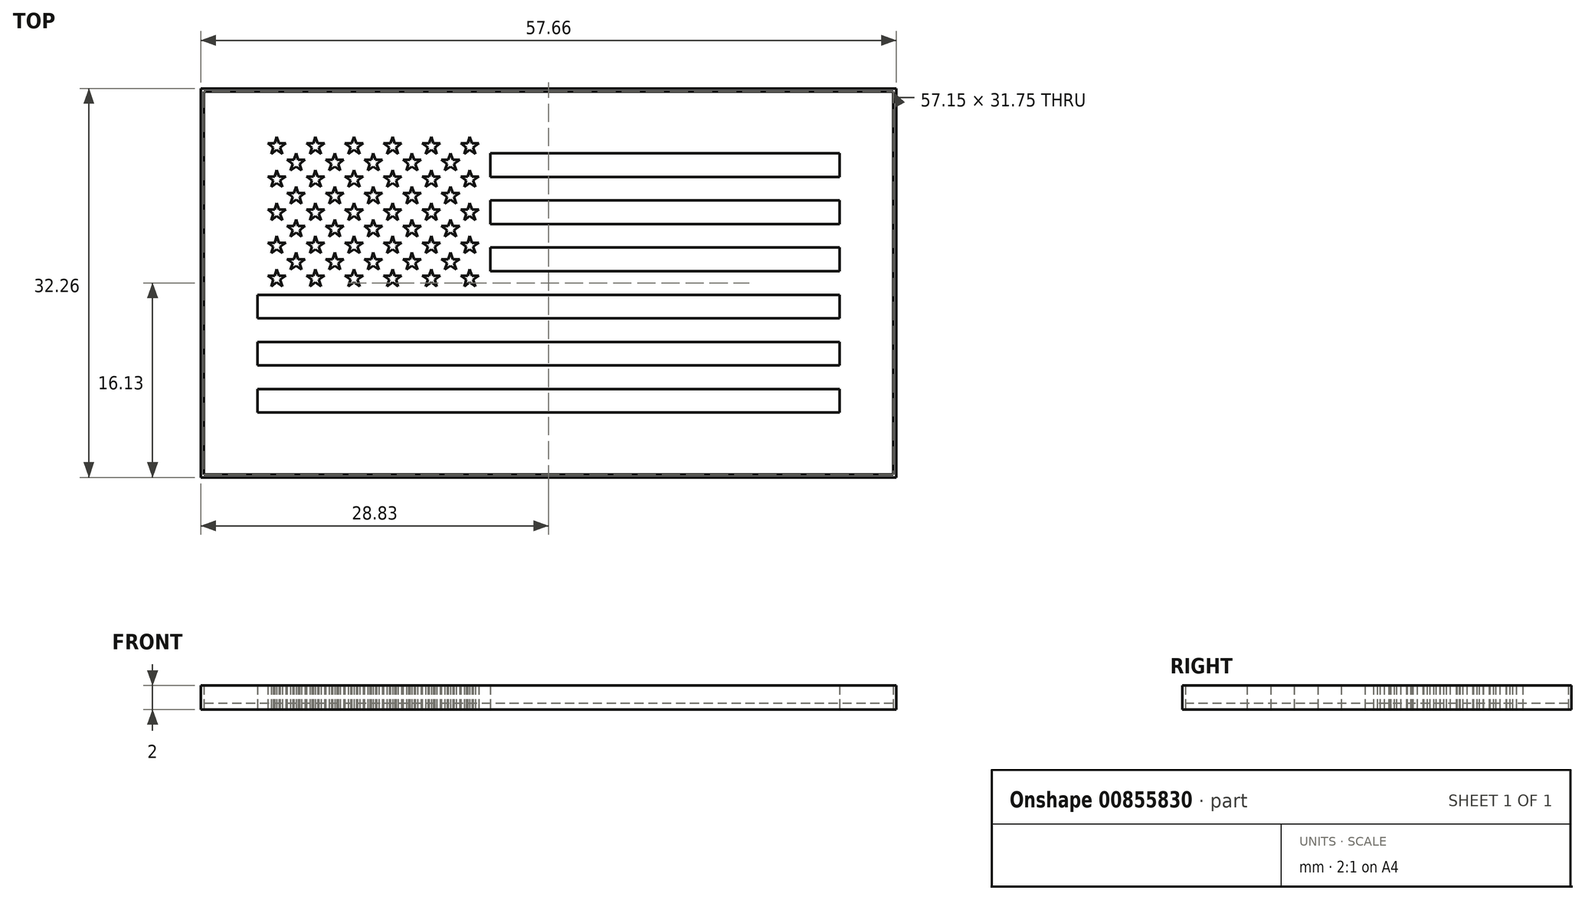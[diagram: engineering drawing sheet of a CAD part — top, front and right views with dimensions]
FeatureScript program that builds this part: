
annotation { "Feature Type Name" : "Feature", "Feature Type Description" : "" }
export const myFeature = defineFeature(function(context is Context, id is Id, definition is map)
    precondition{}
    {
        {
            var Q0;
            Q0=qCreatedBy(makeId("Top.planeOp"),FACE);
            var sketch = newSketch(context, id + "F0", { "sketchPlane" : qUnion([Q0])});
            skLineSegment(sketch, "E0.rect.bottom", {"start": v(24.13, 12.7) * mm, "end": v(-24.13, 12.7) * mm});
            skLineSegment(sketch, "E0.rect.top", {"start": v(24.13, -12.7) * mm, "end": v(-24.13, -12.7) * mm});
            skLineSegment(sketch, "E0.rect.left", {"start": v(24.13, 12.7) * mm, "end": v(24.13, -12.7) * mm});
            skLineSegment(sketch, "E0.rect.right", {"start": v(-24.13, 12.7) * mm, "end": v(-24.13, -12.7) * mm});
            skPoint(sketch, "E0.rect.middle", {"position": v(0, 0) * mm});
            skLineSegment(sketch, "E1.bottom", {"start": v(-24.13, 12.7) * mm, "end": v(-4.83, 12.7) * mm});
            skLineSegment(sketch, "E1.top", {"start": v(-24.13, -0.98) * mm, "end": v(-4.83, -0.98) * mm});
            skLineSegment(sketch, "E1.left", {"start": v(-24.13, 12.7) * mm, "end": v(-24.13, -0.98) * mm});
            skLineSegment(sketch, "E1.right", {"start": v(-4.83, 12.7) * mm, "end": v(-4.83, -0.98) * mm});
            skLineSegment(sketch, "E2.bottom", {"start": v(-4.83, 12.7) * mm, "end": v(24.13, 12.7) * mm});
            skLineSegment(sketch, "E2.top", {"start": v(-4.83, 10.75) * mm, "end": v(24.13, 10.75) * mm});
            skLineSegment(sketch, "E2.left", {"start": v(-4.83, 12.7) * mm, "end": v(-4.83, 10.75) * mm});
            skLineSegment(sketch, "E2.right", {"start": v(24.13, 12.7) * mm, "end": v(24.13, 10.75) * mm});
            skLineSegment(sketch, "E3.MirrorCS", {"start": v(-4.83, 8.8) * mm, "end": v(24.13, 8.8) * mm});
            skLineSegment(sketch, "E4.MirrorCS", {"start": v(-4.83, 6.84) * mm, "end": v(24.13, 6.84) * mm});
            skLineSegment(sketch, "E5.MirrorCS", {"start": v(-4.83, 4.89) * mm, "end": v(24.13, 4.89) * mm});
            skLineSegment(sketch, "E6.MirrorCS", {"start": v(-4.83, 2.93) * mm, "end": v(24.13, 2.93) * mm});
            skLineSegment(sketch, "E7.MirrorCS", {"start": v(-4.83, 0.98) * mm, "end": v(24.13, 0.98) * mm});
            skLineSegment(sketch, "E8.MirrorCS", {"start": v(-4.83, -0.97) * mm, "end": v(24.13, -0.97) * mm});
            skLineSegment(sketch, "E9.bottom", {"start": v(-24.13, -0.98) * mm, "end": v(24.13, -0.98) * mm});
            skLineSegment(sketch, "E9.top", {"start": v(-24.13, -2.93) * mm, "end": v(24.13, -2.93) * mm});
            skLineSegment(sketch, "E9.left", {"start": v(-24.13, -0.98) * mm, "end": v(-24.13, -2.93) * mm});
            skLineSegment(sketch, "E9.right", {"start": v(24.13, -0.98) * mm, "end": v(24.13, -2.93) * mm});
            skLineSegment(sketch, "E10.MirrorCS", {"start": v(-24.13, -4.88) * mm, "end": v(24.13, -4.88) * mm});
            skLineSegment(sketch, "E11.MirrorCS", {"start": v(-24.13, -6.84) * mm, "end": v(24.13, -6.84) * mm});
            skLineSegment(sketch, "E12.MirrorCS", {"start": v(-24.13, -8.8) * mm, "end": v(24.13, -8.8) * mm});
            skLineSegment(sketch, "E13.MirrorCS", {"start": v(-24.13, -10.74) * mm, "end": v(24.13, -10.74) * mm});
            skLineSegment(sketch, "E14.bottom", {"start": v(-24.13, 12.7) * mm, "end": v(-22.53, 12.7) * mm});
            skLineSegment(sketch, "E14.left", {"start": v(-24.13, 12.7) * mm, "end": v(-24.13, 11.33) * mm});
            skPoint(sketch, "E15.cCircle.perimeterSnap0", {"position": v(-22.53, 12.01) * mm});
            skPoint(sketch, "E15.0.startSnap0", {"position": v(-22.53, 12.01) * mm});
            skLineSegment(sketch, "E16", {"start": v(-22.53, 12.12) * mm, "end": v(-22.35, 11.57) * mm});
            skLineSegment(sketch, "E17", {"start": v(-21.78, 11.57) * mm, "end": v(-22.35, 11.57) * mm});
            skLineSegment(sketch, "E18", {"start": v(-23, 10.7) * mm, "end": v(-22.82, 11.24) * mm});
            skLineSegment(sketch, "E19", {"start": v(-23.28, 11.57) * mm, "end": v(-22.82, 11.24) * mm});
            skLineSegment(sketch, "E20", {"start": v(-21.78, 11.57) * mm, "end": v(-22.24, 11.24) * mm});
            skLineSegment(sketch, "E21.trimOffspring", {"start": v(-22.24, 11.24) * mm, "end": v(-22.07, 10.7) * mm});
            skLineSegment(sketch, "E22.trimOffspring", {"start": v(-22.53, 11.03) * mm, "end": v(-23, 10.7) * mm});
            skLineSegment(sketch, "E23.trimOffspring", {"start": v(-22.53, 11.03) * mm, "end": v(-22.07, 10.7) * mm});
            skLineSegment(sketch, "E24.trimOffspring", {"start": v(-22.7, 11.57) * mm, "end": v(-22.53, 12.12) * mm});
            skLineSegment(sketch, "E25.trimOffspring", {"start": v(-22.7, 11.57) * mm, "end": v(-23.28, 11.57) * mm});
            skLineSegment(sketch, "E26.0.1.0", {"start": v(-22.53, 9.37) * mm, "end": v(-22.35, 8.83) * mm});
            skLineSegment(sketch, "E26.0.1.1", {"start": v(-21.78, 8.83) * mm, "end": v(-22.35, 8.83) * mm});
            skLineSegment(sketch, "E26.0.1.2", {"start": v(-21.78, 8.83) * mm, "end": v(-22.24, 8.5) * mm});
            skLineSegment(sketch, "E26.0.1.3", {"start": v(-22.24, 8.5) * mm, "end": v(-22.07, 7.95) * mm});
            skLineSegment(sketch, "E26.0.1.4", {"start": v(-22.53, 8.28) * mm, "end": v(-22.07, 7.95) * mm});
            skLineSegment(sketch, "E26.0.1.5", {"start": v(-22.53, 8.28) * mm, "end": v(-23, 7.95) * mm});
            skLineSegment(sketch, "E26.0.1.6", {"start": v(-23, 7.95) * mm, "end": v(-22.82, 8.5) * mm});
            skLineSegment(sketch, "E26.0.1.7", {"start": v(-23.28, 8.83) * mm, "end": v(-22.82, 8.5) * mm});
            skLineSegment(sketch, "E26.0.1.8", {"start": v(-22.7, 8.83) * mm, "end": v(-22.53, 9.37) * mm});
            skLineSegment(sketch, "E26.0.1.9", {"start": v(-22.7, 8.83) * mm, "end": v(-23.28, 8.83) * mm});
            skLineSegment(sketch, "E26.0.2.0", {"start": v(-22.53, 6.63) * mm, "end": v(-22.35, 6.09) * mm});
            skLineSegment(sketch, "E26.0.2.1", {"start": v(-21.78, 6.09) * mm, "end": v(-22.35, 6.09) * mm});
            skLineSegment(sketch, "E26.0.2.2", {"start": v(-21.78, 6.09) * mm, "end": v(-22.24, 5.75) * mm});
            skLineSegment(sketch, "E26.0.2.3", {"start": v(-22.24, 5.75) * mm, "end": v(-22.07, 5.2) * mm});
            skLineSegment(sketch, "E26.0.2.4", {"start": v(-22.53, 5.54) * mm, "end": v(-22.07, 5.2) * mm});
            skLineSegment(sketch, "E26.0.2.5", {"start": v(-22.53, 5.54) * mm, "end": v(-23, 5.2) * mm});
            skLineSegment(sketch, "E26.0.2.6", {"start": v(-23, 5.2) * mm, "end": v(-22.82, 5.75) * mm});
            skLineSegment(sketch, "E26.0.2.7", {"start": v(-23.28, 6.09) * mm, "end": v(-22.82, 5.75) * mm});
            skLineSegment(sketch, "E26.0.2.8", {"start": v(-22.7, 6.09) * mm, "end": v(-22.53, 6.63) * mm});
            skLineSegment(sketch, "E26.0.2.9", {"start": v(-22.7, 6.09) * mm, "end": v(-23.28, 6.09) * mm});
            skLineSegment(sketch, "E26.0.3.0", {"start": v(-22.53, 3.89) * mm, "end": v(-22.35, 3.34) * mm});
            skLineSegment(sketch, "E26.0.3.1", {"start": v(-21.78, 3.34) * mm, "end": v(-22.35, 3.34) * mm});
            skLineSegment(sketch, "E26.0.3.2", {"start": v(-21.78, 3.34) * mm, "end": v(-22.24, 3) * mm});
            skLineSegment(sketch, "E26.0.3.3", {"start": v(-22.24, 3) * mm, "end": v(-22.07, 2.46) * mm});
            skLineSegment(sketch, "E26.0.3.4", {"start": v(-22.53, 2.8) * mm, "end": v(-22.07, 2.46) * mm});
            skLineSegment(sketch, "E26.0.3.5", {"start": v(-22.53, 2.8) * mm, "end": v(-23, 2.46) * mm});
            skLineSegment(sketch, "E26.0.3.6", {"start": v(-23, 2.46) * mm, "end": v(-22.82, 3) * mm});
            skLineSegment(sketch, "E26.0.3.7", {"start": v(-23.28, 3.34) * mm, "end": v(-22.82, 3) * mm});
            skLineSegment(sketch, "E26.0.3.8", {"start": v(-22.7, 3.34) * mm, "end": v(-22.53, 3.89) * mm});
            skLineSegment(sketch, "E26.0.3.9", {"start": v(-22.7, 3.34) * mm, "end": v(-23.28, 3.34) * mm});
            skLineSegment(sketch, "E26.0.4.0", {"start": v(-22.53, 1.14) * mm, "end": v(-22.35, 0.6) * mm});
            skLineSegment(sketch, "E26.0.4.1", {"start": v(-21.78, 0.6) * mm, "end": v(-22.35, 0.6) * mm});
            skLineSegment(sketch, "E26.0.4.2", {"start": v(-21.78, 0.6) * mm, "end": v(-22.24, 0.26) * mm});
            skLineSegment(sketch, "E26.0.4.3", {"start": v(-22.24, 0.26) * mm, "end": v(-22.07, -0.28) * mm});
            skLineSegment(sketch, "E26.0.4.4", {"start": v(-22.53, 0.05) * mm, "end": v(-22.07, -0.28) * mm});
            skLineSegment(sketch, "E26.0.4.5", {"start": v(-22.53, 0.05) * mm, "end": v(-23, -0.28) * mm});
            skLineSegment(sketch, "E26.0.4.6", {"start": v(-23, -0.28) * mm, "end": v(-22.82, 0.26) * mm});
            skLineSegment(sketch, "E26.0.4.7", {"start": v(-23.28, 0.6) * mm, "end": v(-22.82, 0.26) * mm});
            skLineSegment(sketch, "E26.0.4.8", {"start": v(-22.7, 0.6) * mm, "end": v(-22.53, 1.14) * mm});
            skLineSegment(sketch, "E26.0.4.9", {"start": v(-22.7, 0.6) * mm, "end": v(-23.28, 0.6) * mm});
            skLineSegment(sketch, "E26.1.0.0", {"start": v(-19.33, 12.12) * mm, "end": v(-19.15, 11.57) * mm});
            skLineSegment(sketch, "E26.1.0.1", {"start": v(-18.58, 11.57) * mm, "end": v(-19.15, 11.57) * mm});
            skLineSegment(sketch, "E26.1.0.2", {"start": v(-18.58, 11.57) * mm, "end": v(-19.04, 11.24) * mm});
            skLineSegment(sketch, "E26.1.0.3", {"start": v(-19.04, 11.24) * mm, "end": v(-18.87, 10.7) * mm});
            skLineSegment(sketch, "E26.1.0.4", {"start": v(-19.33, 11.03) * mm, "end": v(-18.87, 10.7) * mm});
            skLineSegment(sketch, "E26.1.0.5", {"start": v(-19.33, 11.03) * mm, "end": v(-19.8, 10.7) * mm});
            skLineSegment(sketch, "E26.1.0.6", {"start": v(-19.8, 10.7) * mm, "end": v(-19.62, 11.24) * mm});
            skLineSegment(sketch, "E26.1.0.7", {"start": v(-20.08, 11.57) * mm, "end": v(-19.62, 11.24) * mm});
            skLineSegment(sketch, "E26.1.0.8", {"start": v(-19.5, 11.57) * mm, "end": v(-19.33, 12.12) * mm});
            skLineSegment(sketch, "E26.1.0.9", {"start": v(-19.5, 11.57) * mm, "end": v(-20.08, 11.57) * mm});
            skLineSegment(sketch, "E26.1.1.0", {"start": v(-19.33, 9.37) * mm, "end": v(-19.15, 8.83) * mm});
            skLineSegment(sketch, "E26.1.1.1", {"start": v(-18.58, 8.83) * mm, "end": v(-19.15, 8.83) * mm});
            skLineSegment(sketch, "E26.1.1.2", {"start": v(-18.58, 8.83) * mm, "end": v(-19.04, 8.5) * mm});
            skLineSegment(sketch, "E26.1.1.3", {"start": v(-19.04, 8.5) * mm, "end": v(-18.87, 7.95) * mm});
            skLineSegment(sketch, "E26.1.1.4", {"start": v(-19.33, 8.28) * mm, "end": v(-18.87, 7.95) * mm});
            skLineSegment(sketch, "E26.1.1.5", {"start": v(-19.33, 8.28) * mm, "end": v(-19.8, 7.95) * mm});
            skLineSegment(sketch, "E26.1.1.6", {"start": v(-19.8, 7.95) * mm, "end": v(-19.62, 8.5) * mm});
            skLineSegment(sketch, "E26.1.1.7", {"start": v(-20.08, 8.83) * mm, "end": v(-19.62, 8.5) * mm});
            skLineSegment(sketch, "E26.1.1.8", {"start": v(-19.5, 8.83) * mm, "end": v(-19.33, 9.37) * mm});
            skLineSegment(sketch, "E26.1.1.9", {"start": v(-19.5, 8.83) * mm, "end": v(-20.08, 8.83) * mm});
            skLineSegment(sketch, "E26.1.2.0", {"start": v(-19.33, 6.63) * mm, "end": v(-19.15, 6.09) * mm});
            skLineSegment(sketch, "E26.1.2.1", {"start": v(-18.58, 6.09) * mm, "end": v(-19.15, 6.09) * mm});
            skLineSegment(sketch, "E26.1.2.2", {"start": v(-18.58, 6.09) * mm, "end": v(-19.04, 5.75) * mm});
            skLineSegment(sketch, "E26.1.2.3", {"start": v(-19.04, 5.75) * mm, "end": v(-18.87, 5.2) * mm});
            skLineSegment(sketch, "E26.1.2.4", {"start": v(-19.33, 5.54) * mm, "end": v(-18.87, 5.2) * mm});
            skLineSegment(sketch, "E26.1.2.5", {"start": v(-19.33, 5.54) * mm, "end": v(-19.8, 5.2) * mm});
            skLineSegment(sketch, "E26.1.2.6", {"start": v(-19.8, 5.2) * mm, "end": v(-19.62, 5.75) * mm});
            skLineSegment(sketch, "E26.1.2.7", {"start": v(-20.08, 6.09) * mm, "end": v(-19.62, 5.75) * mm});
            skLineSegment(sketch, "E26.1.2.8", {"start": v(-19.5, 6.09) * mm, "end": v(-19.33, 6.63) * mm});
            skLineSegment(sketch, "E26.1.2.9", {"start": v(-19.5, 6.09) * mm, "end": v(-20.08, 6.09) * mm});
            skLineSegment(sketch, "E26.1.3.0", {"start": v(-19.33, 3.89) * mm, "end": v(-19.15, 3.34) * mm});
            skLineSegment(sketch, "E26.1.3.1", {"start": v(-18.58, 3.34) * mm, "end": v(-19.15, 3.34) * mm});
            skLineSegment(sketch, "E26.1.3.2", {"start": v(-18.58, 3.34) * mm, "end": v(-19.04, 3) * mm});
            skLineSegment(sketch, "E26.1.3.3", {"start": v(-19.04, 3) * mm, "end": v(-18.87, 2.46) * mm});
            skLineSegment(sketch, "E26.1.3.4", {"start": v(-19.33, 2.8) * mm, "end": v(-18.87, 2.46) * mm});
            skLineSegment(sketch, "E26.1.3.5", {"start": v(-19.33, 2.8) * mm, "end": v(-19.8, 2.46) * mm});
            skLineSegment(sketch, "E26.1.3.6", {"start": v(-19.8, 2.46) * mm, "end": v(-19.62, 3) * mm});
            skLineSegment(sketch, "E26.1.3.7", {"start": v(-20.08, 3.34) * mm, "end": v(-19.62, 3) * mm});
            skLineSegment(sketch, "E26.1.3.8", {"start": v(-19.5, 3.34) * mm, "end": v(-19.33, 3.89) * mm});
            skLineSegment(sketch, "E26.1.3.9", {"start": v(-19.5, 3.34) * mm, "end": v(-20.08, 3.34) * mm});
            skLineSegment(sketch, "E26.1.4.0", {"start": v(-19.33, 1.14) * mm, "end": v(-19.15, 0.6) * mm});
            skLineSegment(sketch, "E26.1.4.1", {"start": v(-18.58, 0.6) * mm, "end": v(-19.15, 0.6) * mm});
            skLineSegment(sketch, "E26.1.4.2", {"start": v(-18.58, 0.6) * mm, "end": v(-19.04, 0.26) * mm});
            skLineSegment(sketch, "E26.1.4.3", {"start": v(-19.04, 0.26) * mm, "end": v(-18.87, -0.28) * mm});
            skLineSegment(sketch, "E26.1.4.4", {"start": v(-19.33, 0.05) * mm, "end": v(-18.87, -0.28) * mm});
            skLineSegment(sketch, "E26.1.4.5", {"start": v(-19.33, 0.05) * mm, "end": v(-19.8, -0.28) * mm});
            skLineSegment(sketch, "E26.1.4.6", {"start": v(-19.8, -0.28) * mm, "end": v(-19.62, 0.26) * mm});
            skLineSegment(sketch, "E26.1.4.7", {"start": v(-20.08, 0.6) * mm, "end": v(-19.62, 0.26) * mm});
            skLineSegment(sketch, "E26.1.4.8", {"start": v(-19.5, 0.6) * mm, "end": v(-19.33, 1.14) * mm});
            skLineSegment(sketch, "E26.1.4.9", {"start": v(-19.5, 0.6) * mm, "end": v(-20.08, 0.6) * mm});
            skLineSegment(sketch, "E26.2.0.0", {"start": v(-16.13, 12.12) * mm, "end": v(-15.95, 11.57) * mm});
            skLineSegment(sketch, "E26.2.0.1", {"start": v(-15.38, 11.57) * mm, "end": v(-15.95, 11.57) * mm});
            skLineSegment(sketch, "E26.2.0.2", {"start": v(-15.38, 11.57) * mm, "end": v(-15.84, 11.24) * mm});
            skLineSegment(sketch, "E26.2.0.3", {"start": v(-15.84, 11.24) * mm, "end": v(-15.67, 10.7) * mm});
            skLineSegment(sketch, "E26.2.0.4", {"start": v(-16.13, 11.03) * mm, "end": v(-15.67, 10.7) * mm});
            skLineSegment(sketch, "E26.2.0.5", {"start": v(-16.13, 11.03) * mm, "end": v(-16.6, 10.7) * mm});
            skLineSegment(sketch, "E26.2.0.6", {"start": v(-16.6, 10.7) * mm, "end": v(-16.42, 11.24) * mm});
            skLineSegment(sketch, "E26.2.0.7", {"start": v(-16.88, 11.57) * mm, "end": v(-16.42, 11.24) * mm});
            skLineSegment(sketch, "E26.2.0.8", {"start": v(-16.3, 11.57) * mm, "end": v(-16.13, 12.12) * mm});
            skLineSegment(sketch, "E26.2.0.9", {"start": v(-16.3, 11.57) * mm, "end": v(-16.88, 11.57) * mm});
            skLineSegment(sketch, "E26.2.1.0", {"start": v(-16.13, 9.37) * mm, "end": v(-15.95, 8.83) * mm});
            skLineSegment(sketch, "E26.2.1.1", {"start": v(-15.38, 8.83) * mm, "end": v(-15.95, 8.83) * mm});
            skLineSegment(sketch, "E26.2.1.2", {"start": v(-15.38, 8.83) * mm, "end": v(-15.84, 8.5) * mm});
            skLineSegment(sketch, "E26.2.1.3", {"start": v(-15.84, 8.5) * mm, "end": v(-15.67, 7.95) * mm});
            skLineSegment(sketch, "E26.2.1.4", {"start": v(-16.13, 8.28) * mm, "end": v(-15.67, 7.95) * mm});
            skLineSegment(sketch, "E26.2.1.5", {"start": v(-16.13, 8.28) * mm, "end": v(-16.6, 7.95) * mm});
            skLineSegment(sketch, "E26.2.1.6", {"start": v(-16.6, 7.95) * mm, "end": v(-16.42, 8.5) * mm});
            skLineSegment(sketch, "E26.2.1.7", {"start": v(-16.88, 8.83) * mm, "end": v(-16.42, 8.5) * mm});
            skLineSegment(sketch, "E26.2.1.8", {"start": v(-16.3, 8.83) * mm, "end": v(-16.13, 9.37) * mm});
            skLineSegment(sketch, "E26.2.1.9", {"start": v(-16.3, 8.83) * mm, "end": v(-16.88, 8.83) * mm});
            skLineSegment(sketch, "E26.2.2.0", {"start": v(-16.13, 6.63) * mm, "end": v(-15.95, 6.09) * mm});
            skLineSegment(sketch, "E26.2.2.1", {"start": v(-15.38, 6.09) * mm, "end": v(-15.95, 6.09) * mm});
            skLineSegment(sketch, "E26.2.2.2", {"start": v(-15.38, 6.09) * mm, "end": v(-15.84, 5.75) * mm});
            skLineSegment(sketch, "E26.2.2.3", {"start": v(-15.84, 5.75) * mm, "end": v(-15.67, 5.2) * mm});
            skLineSegment(sketch, "E26.2.2.4", {"start": v(-16.13, 5.54) * mm, "end": v(-15.67, 5.2) * mm});
            skLineSegment(sketch, "E26.2.2.5", {"start": v(-16.13, 5.54) * mm, "end": v(-16.6, 5.2) * mm});
            skLineSegment(sketch, "E26.2.2.6", {"start": v(-16.6, 5.2) * mm, "end": v(-16.42, 5.75) * mm});
            skLineSegment(sketch, "E26.2.2.7", {"start": v(-16.88, 6.09) * mm, "end": v(-16.42, 5.75) * mm});
            skLineSegment(sketch, "E26.2.2.8", {"start": v(-16.3, 6.09) * mm, "end": v(-16.13, 6.63) * mm});
            skLineSegment(sketch, "E26.2.2.9", {"start": v(-16.3, 6.09) * mm, "end": v(-16.88, 6.09) * mm});
            skLineSegment(sketch, "E26.2.3.0", {"start": v(-16.13, 3.89) * mm, "end": v(-15.95, 3.34) * mm});
            skLineSegment(sketch, "E26.2.3.1", {"start": v(-15.38, 3.34) * mm, "end": v(-15.95, 3.34) * mm});
            skLineSegment(sketch, "E26.2.3.2", {"start": v(-15.38, 3.34) * mm, "end": v(-15.84, 3) * mm});
            skLineSegment(sketch, "E26.2.3.3", {"start": v(-15.84, 3) * mm, "end": v(-15.67, 2.46) * mm});
            skLineSegment(sketch, "E26.2.3.4", {"start": v(-16.13, 2.8) * mm, "end": v(-15.67, 2.46) * mm});
            skLineSegment(sketch, "E26.2.3.5", {"start": v(-16.13, 2.8) * mm, "end": v(-16.6, 2.46) * mm});
            skLineSegment(sketch, "E26.2.3.6", {"start": v(-16.6, 2.46) * mm, "end": v(-16.42, 3) * mm});
            skLineSegment(sketch, "E26.2.3.7", {"start": v(-16.88, 3.34) * mm, "end": v(-16.42, 3) * mm});
            skLineSegment(sketch, "E26.2.3.8", {"start": v(-16.3, 3.34) * mm, "end": v(-16.13, 3.89) * mm});
            skLineSegment(sketch, "E26.2.3.9", {"start": v(-16.3, 3.34) * mm, "end": v(-16.88, 3.34) * mm});
            skLineSegment(sketch, "E26.2.4.0", {"start": v(-16.13, 1.14) * mm, "end": v(-15.95, 0.6) * mm});
            skLineSegment(sketch, "E26.2.4.1", {"start": v(-15.38, 0.6) * mm, "end": v(-15.95, 0.6) * mm});
            skLineSegment(sketch, "E26.2.4.2", {"start": v(-15.38, 0.6) * mm, "end": v(-15.84, 0.26) * mm});
            skLineSegment(sketch, "E26.2.4.3", {"start": v(-15.84, 0.26) * mm, "end": v(-15.67, -0.28) * mm});
            skLineSegment(sketch, "E26.2.4.4", {"start": v(-16.13, 0.05) * mm, "end": v(-15.67, -0.28) * mm});
            skLineSegment(sketch, "E26.2.4.5", {"start": v(-16.13, 0.05) * mm, "end": v(-16.6, -0.28) * mm});
            skLineSegment(sketch, "E26.2.4.6", {"start": v(-16.6, -0.28) * mm, "end": v(-16.42, 0.26) * mm});
            skLineSegment(sketch, "E26.2.4.7", {"start": v(-16.88, 0.6) * mm, "end": v(-16.42, 0.26) * mm});
            skLineSegment(sketch, "E26.2.4.8", {"start": v(-16.3, 0.6) * mm, "end": v(-16.13, 1.14) * mm});
            skLineSegment(sketch, "E26.2.4.9", {"start": v(-16.3, 0.6) * mm, "end": v(-16.88, 0.6) * mm});
            skLineSegment(sketch, "E26.3.0.0", {"start": v(-12.93, 12.12) * mm, "end": v(-12.75, 11.57) * mm});
            skLineSegment(sketch, "E26.3.0.1", {"start": v(-12.18, 11.57) * mm, "end": v(-12.75, 11.57) * mm});
            skLineSegment(sketch, "E26.3.0.2", {"start": v(-12.18, 11.57) * mm, "end": v(-12.64, 11.24) * mm});
            skLineSegment(sketch, "E26.3.0.3", {"start": v(-12.64, 11.24) * mm, "end": v(-12.47, 10.7) * mm});
            skLineSegment(sketch, "E26.3.0.4", {"start": v(-12.93, 11.03) * mm, "end": v(-12.47, 10.7) * mm});
            skLineSegment(sketch, "E26.3.0.5", {"start": v(-12.93, 11.03) * mm, "end": v(-13.4, 10.7) * mm});
            skLineSegment(sketch, "E26.3.0.6", {"start": v(-13.4, 10.7) * mm, "end": v(-13.21, 11.24) * mm});
            skLineSegment(sketch, "E26.3.0.7", {"start": v(-13.68, 11.57) * mm, "end": v(-13.21, 11.24) * mm});
            skLineSegment(sketch, "E26.3.0.8", {"start": v(-13.1, 11.57) * mm, "end": v(-12.93, 12.12) * mm});
            skLineSegment(sketch, "E26.3.0.9", {"start": v(-13.1, 11.57) * mm, "end": v(-13.68, 11.57) * mm});
            skLineSegment(sketch, "E26.3.1.0", {"start": v(-12.93, 9.37) * mm, "end": v(-12.75, 8.83) * mm});
            skLineSegment(sketch, "E26.3.1.1", {"start": v(-12.18, 8.83) * mm, "end": v(-12.75, 8.83) * mm});
            skLineSegment(sketch, "E26.3.1.2", {"start": v(-12.18, 8.83) * mm, "end": v(-12.64, 8.5) * mm});
            skLineSegment(sketch, "E26.3.1.3", {"start": v(-12.64, 8.5) * mm, "end": v(-12.47, 7.95) * mm});
            skLineSegment(sketch, "E26.3.1.4", {"start": v(-12.93, 8.28) * mm, "end": v(-12.47, 7.95) * mm});
            skLineSegment(sketch, "E26.3.1.5", {"start": v(-12.93, 8.28) * mm, "end": v(-13.4, 7.95) * mm});
            skLineSegment(sketch, "E26.3.1.6", {"start": v(-13.4, 7.95) * mm, "end": v(-13.21, 8.5) * mm});
            skLineSegment(sketch, "E26.3.1.7", {"start": v(-13.68, 8.83) * mm, "end": v(-13.21, 8.5) * mm});
            skLineSegment(sketch, "E26.3.1.8", {"start": v(-13.1, 8.83) * mm, "end": v(-12.93, 9.37) * mm});
            skLineSegment(sketch, "E26.3.1.9", {"start": v(-13.1, 8.83) * mm, "end": v(-13.68, 8.83) * mm});
            skLineSegment(sketch, "E26.3.2.0", {"start": v(-12.93, 6.63) * mm, "end": v(-12.75, 6.09) * mm});
            skLineSegment(sketch, "E26.3.2.1", {"start": v(-12.18, 6.09) * mm, "end": v(-12.75, 6.09) * mm});
            skLineSegment(sketch, "E26.3.2.2", {"start": v(-12.18, 6.09) * mm, "end": v(-12.64, 5.75) * mm});
            skLineSegment(sketch, "E26.3.2.3", {"start": v(-12.64, 5.75) * mm, "end": v(-12.47, 5.2) * mm});
            skLineSegment(sketch, "E26.3.2.4", {"start": v(-12.93, 5.54) * mm, "end": v(-12.47, 5.2) * mm});
            skLineSegment(sketch, "E26.3.2.5", {"start": v(-12.93, 5.54) * mm, "end": v(-13.4, 5.2) * mm});
            skLineSegment(sketch, "E26.3.2.6", {"start": v(-13.4, 5.2) * mm, "end": v(-13.21, 5.75) * mm});
            skLineSegment(sketch, "E26.3.2.7", {"start": v(-13.68, 6.09) * mm, "end": v(-13.21, 5.75) * mm});
            skLineSegment(sketch, "E26.3.2.8", {"start": v(-13.1, 6.09) * mm, "end": v(-12.93, 6.63) * mm});
            skLineSegment(sketch, "E26.3.2.9", {"start": v(-13.1, 6.09) * mm, "end": v(-13.68, 6.09) * mm});
            skLineSegment(sketch, "E26.3.3.0", {"start": v(-12.93, 3.89) * mm, "end": v(-12.75, 3.34) * mm});
            skLineSegment(sketch, "E26.3.3.1", {"start": v(-12.18, 3.34) * mm, "end": v(-12.75, 3.34) * mm});
            skLineSegment(sketch, "E26.3.3.2", {"start": v(-12.18, 3.34) * mm, "end": v(-12.64, 3) * mm});
            skLineSegment(sketch, "E26.3.3.3", {"start": v(-12.64, 3) * mm, "end": v(-12.47, 2.46) * mm});
            skLineSegment(sketch, "E26.3.3.4", {"start": v(-12.93, 2.8) * mm, "end": v(-12.47, 2.46) * mm});
            skLineSegment(sketch, "E26.3.3.5", {"start": v(-12.93, 2.8) * mm, "end": v(-13.4, 2.46) * mm});
            skLineSegment(sketch, "E26.3.3.6", {"start": v(-13.4, 2.46) * mm, "end": v(-13.21, 3) * mm});
            skLineSegment(sketch, "E26.3.3.7", {"start": v(-13.68, 3.34) * mm, "end": v(-13.21, 3) * mm});
            skLineSegment(sketch, "E26.3.3.8", {"start": v(-13.1, 3.34) * mm, "end": v(-12.93, 3.89) * mm});
            skLineSegment(sketch, "E26.3.3.9", {"start": v(-13.1, 3.34) * mm, "end": v(-13.68, 3.34) * mm});
            skLineSegment(sketch, "E26.3.4.0", {"start": v(-12.93, 1.14) * mm, "end": v(-12.75, 0.6) * mm});
            skLineSegment(sketch, "E26.3.4.1", {"start": v(-12.18, 0.6) * mm, "end": v(-12.75, 0.6) * mm});
            skLineSegment(sketch, "E26.3.4.2", {"start": v(-12.18, 0.6) * mm, "end": v(-12.64, 0.26) * mm});
            skLineSegment(sketch, "E26.3.4.3", {"start": v(-12.64, 0.26) * mm, "end": v(-12.47, -0.28) * mm});
            skLineSegment(sketch, "E26.3.4.4", {"start": v(-12.93, 0.05) * mm, "end": v(-12.47, -0.28) * mm});
            skLineSegment(sketch, "E26.3.4.5", {"start": v(-12.93, 0.05) * mm, "end": v(-13.4, -0.28) * mm});
            skLineSegment(sketch, "E26.3.4.6", {"start": v(-13.4, -0.28) * mm, "end": v(-13.21, 0.26) * mm});
            skLineSegment(sketch, "E26.3.4.7", {"start": v(-13.68, 0.6) * mm, "end": v(-13.21, 0.26) * mm});
            skLineSegment(sketch, "E26.3.4.8", {"start": v(-13.1, 0.6) * mm, "end": v(-12.93, 1.14) * mm});
            skLineSegment(sketch, "E26.3.4.9", {"start": v(-13.1, 0.6) * mm, "end": v(-13.68, 0.6) * mm});
            skLineSegment(sketch, "E26.4.0.0", {"start": v(-9.73, 12.12) * mm, "end": v(-9.55, 11.57) * mm});
            skLineSegment(sketch, "E26.4.0.1", {"start": v(-8.98, 11.57) * mm, "end": v(-9.55, 11.57) * mm});
            skLineSegment(sketch, "E26.4.0.2", {"start": v(-8.98, 11.57) * mm, "end": v(-9.44, 11.24) * mm});
            skLineSegment(sketch, "E26.4.0.3", {"start": v(-9.44, 11.24) * mm, "end": v(-9.27, 10.7) * mm});
            skLineSegment(sketch, "E26.4.0.4", {"start": v(-9.73, 11.03) * mm, "end": v(-9.27, 10.7) * mm});
            skLineSegment(sketch, "E26.4.0.5", {"start": v(-9.73, 11.03) * mm, "end": v(-10.2, 10.7) * mm});
            skLineSegment(sketch, "E26.4.0.6", {"start": v(-10.2, 10.7) * mm, "end": v(-10.01, 11.24) * mm});
            skLineSegment(sketch, "E26.4.0.7", {"start": v(-10.48, 11.57) * mm, "end": v(-10.01, 11.24) * mm});
            skLineSegment(sketch, "E26.4.0.8", {"start": v(-9.9, 11.57) * mm, "end": v(-9.73, 12.12) * mm});
            skLineSegment(sketch, "E26.4.0.9", {"start": v(-9.9, 11.57) * mm, "end": v(-10.48, 11.57) * mm});
            skLineSegment(sketch, "E26.4.1.0", {"start": v(-9.73, 9.37) * mm, "end": v(-9.55, 8.83) * mm});
            skLineSegment(sketch, "E26.4.1.1", {"start": v(-8.98, 8.83) * mm, "end": v(-9.55, 8.83) * mm});
            skLineSegment(sketch, "E26.4.1.2", {"start": v(-8.98, 8.83) * mm, "end": v(-9.44, 8.5) * mm});
            skLineSegment(sketch, "E26.4.1.3", {"start": v(-9.44, 8.5) * mm, "end": v(-9.27, 7.95) * mm});
            skLineSegment(sketch, "E26.4.1.4", {"start": v(-9.73, 8.28) * mm, "end": v(-9.27, 7.95) * mm});
            skLineSegment(sketch, "E26.4.1.5", {"start": v(-9.73, 8.28) * mm, "end": v(-10.2, 7.95) * mm});
            skLineSegment(sketch, "E26.4.1.6", {"start": v(-10.2, 7.95) * mm, "end": v(-10.01, 8.5) * mm});
            skLineSegment(sketch, "E26.4.1.7", {"start": v(-10.48, 8.83) * mm, "end": v(-10.01, 8.5) * mm});
            skLineSegment(sketch, "E26.4.1.8", {"start": v(-9.9, 8.83) * mm, "end": v(-9.73, 9.37) * mm});
            skLineSegment(sketch, "E26.4.1.9", {"start": v(-9.9, 8.83) * mm, "end": v(-10.48, 8.83) * mm});
            skLineSegment(sketch, "E26.4.2.0", {"start": v(-9.73, 6.63) * mm, "end": v(-9.55, 6.09) * mm});
            skLineSegment(sketch, "E26.4.2.1", {"start": v(-8.98, 6.09) * mm, "end": v(-9.55, 6.09) * mm});
            skLineSegment(sketch, "E26.4.2.2", {"start": v(-8.98, 6.09) * mm, "end": v(-9.44, 5.75) * mm});
            skLineSegment(sketch, "E26.4.2.3", {"start": v(-9.44, 5.75) * mm, "end": v(-9.27, 5.2) * mm});
            skLineSegment(sketch, "E26.4.2.4", {"start": v(-9.73, 5.54) * mm, "end": v(-9.27, 5.2) * mm});
            skLineSegment(sketch, "E26.4.2.5", {"start": v(-9.73, 5.54) * mm, "end": v(-10.2, 5.2) * mm});
            skLineSegment(sketch, "E26.4.2.6", {"start": v(-10.2, 5.2) * mm, "end": v(-10.01, 5.75) * mm});
            skLineSegment(sketch, "E26.4.2.7", {"start": v(-10.48, 6.09) * mm, "end": v(-10.01, 5.75) * mm});
            skLineSegment(sketch, "E26.4.2.8", {"start": v(-9.9, 6.09) * mm, "end": v(-9.73, 6.63) * mm});
            skLineSegment(sketch, "E26.4.2.9", {"start": v(-9.9, 6.09) * mm, "end": v(-10.48, 6.09) * mm});
            skLineSegment(sketch, "E26.4.3.0", {"start": v(-9.73, 3.89) * mm, "end": v(-9.55, 3.34) * mm});
            skLineSegment(sketch, "E26.4.3.1", {"start": v(-8.98, 3.34) * mm, "end": v(-9.55, 3.34) * mm});
            skLineSegment(sketch, "E26.4.3.2", {"start": v(-8.98, 3.34) * mm, "end": v(-9.44, 3) * mm});
            skLineSegment(sketch, "E26.4.3.3", {"start": v(-9.44, 3) * mm, "end": v(-9.27, 2.46) * mm});
            skLineSegment(sketch, "E26.4.3.4", {"start": v(-9.73, 2.8) * mm, "end": v(-9.27, 2.46) * mm});
            skLineSegment(sketch, "E26.4.3.5", {"start": v(-9.73, 2.8) * mm, "end": v(-10.2, 2.46) * mm});
            skLineSegment(sketch, "E26.4.3.6", {"start": v(-10.2, 2.46) * mm, "end": v(-10.01, 3) * mm});
            skLineSegment(sketch, "E26.4.3.7", {"start": v(-10.48, 3.34) * mm, "end": v(-10.01, 3) * mm});
            skLineSegment(sketch, "E26.4.3.8", {"start": v(-9.9, 3.34) * mm, "end": v(-9.73, 3.89) * mm});
            skLineSegment(sketch, "E26.4.3.9", {"start": v(-9.9, 3.34) * mm, "end": v(-10.48, 3.34) * mm});
            skLineSegment(sketch, "E26.4.4.0", {"start": v(-9.73, 1.14) * mm, "end": v(-9.55, 0.6) * mm});
            skLineSegment(sketch, "E26.4.4.1", {"start": v(-8.98, 0.6) * mm, "end": v(-9.55, 0.6) * mm});
            skLineSegment(sketch, "E26.4.4.2", {"start": v(-8.98, 0.6) * mm, "end": v(-9.44, 0.26) * mm});
            skLineSegment(sketch, "E26.4.4.3", {"start": v(-9.44, 0.26) * mm, "end": v(-9.27, -0.28) * mm});
            skLineSegment(sketch, "E26.4.4.4", {"start": v(-9.73, 0.05) * mm, "end": v(-9.27, -0.28) * mm});
            skLineSegment(sketch, "E26.4.4.5", {"start": v(-9.73, 0.05) * mm, "end": v(-10.2, -0.28) * mm});
            skLineSegment(sketch, "E26.4.4.6", {"start": v(-10.2, -0.28) * mm, "end": v(-10.01, 0.26) * mm});
            skLineSegment(sketch, "E26.4.4.7", {"start": v(-10.48, 0.6) * mm, "end": v(-10.01, 0.26) * mm});
            skLineSegment(sketch, "E26.4.4.8", {"start": v(-9.9, 0.6) * mm, "end": v(-9.73, 1.14) * mm});
            skLineSegment(sketch, "E26.4.4.9", {"start": v(-9.9, 0.6) * mm, "end": v(-10.48, 0.6) * mm});
            skLineSegment(sketch, "E26.5.0.0", {"start": v(-6.53, 12.12) * mm, "end": v(-6.35, 11.57) * mm});
            skLineSegment(sketch, "E26.5.0.1", {"start": v(-5.78, 11.57) * mm, "end": v(-6.35, 11.57) * mm});
            skLineSegment(sketch, "E26.5.0.2", {"start": v(-5.78, 11.57) * mm, "end": v(-6.24, 11.24) * mm});
            skLineSegment(sketch, "E26.5.0.3", {"start": v(-6.24, 11.24) * mm, "end": v(-6.06, 10.7) * mm});
            skLineSegment(sketch, "E26.5.0.4", {"start": v(-6.53, 11.03) * mm, "end": v(-6.06, 10.7) * mm});
            skLineSegment(sketch, "E26.5.0.5", {"start": v(-6.53, 11.03) * mm, "end": v(-7, 10.7) * mm});
            skLineSegment(sketch, "E26.5.0.6", {"start": v(-7, 10.7) * mm, "end": v(-6.81, 11.24) * mm});
            skLineSegment(sketch, "E26.5.0.7", {"start": v(-7.28, 11.57) * mm, "end": v(-6.81, 11.24) * mm});
            skLineSegment(sketch, "E26.5.0.8", {"start": v(-6.7, 11.57) * mm, "end": v(-6.53, 12.12) * mm});
            skLineSegment(sketch, "E26.5.0.9", {"start": v(-6.7, 11.57) * mm, "end": v(-7.28, 11.57) * mm});
            skLineSegment(sketch, "E26.5.1.0", {"start": v(-6.53, 9.37) * mm, "end": v(-6.35, 8.83) * mm});
            skLineSegment(sketch, "E26.5.1.1", {"start": v(-5.78, 8.83) * mm, "end": v(-6.35, 8.83) * mm});
            skLineSegment(sketch, "E26.5.1.2", {"start": v(-5.78, 8.83) * mm, "end": v(-6.24, 8.5) * mm});
            skLineSegment(sketch, "E26.5.1.3", {"start": v(-6.24, 8.5) * mm, "end": v(-6.06, 7.95) * mm});
            skLineSegment(sketch, "E26.5.1.4", {"start": v(-6.53, 8.28) * mm, "end": v(-6.06, 7.95) * mm});
            skLineSegment(sketch, "E26.5.1.5", {"start": v(-6.53, 8.28) * mm, "end": v(-7, 7.95) * mm});
            skLineSegment(sketch, "E26.5.1.6", {"start": v(-7, 7.95) * mm, "end": v(-6.81, 8.5) * mm});
            skLineSegment(sketch, "E26.5.1.7", {"start": v(-7.28, 8.83) * mm, "end": v(-6.81, 8.5) * mm});
            skLineSegment(sketch, "E26.5.1.8", {"start": v(-6.7, 8.83) * mm, "end": v(-6.53, 9.37) * mm});
            skLineSegment(sketch, "E26.5.1.9", {"start": v(-6.7, 8.83) * mm, "end": v(-7.28, 8.83) * mm});
            skLineSegment(sketch, "E26.5.2.0", {"start": v(-6.53, 6.63) * mm, "end": v(-6.35, 6.09) * mm});
            skLineSegment(sketch, "E26.5.2.1", {"start": v(-5.78, 6.09) * mm, "end": v(-6.35, 6.09) * mm});
            skLineSegment(sketch, "E26.5.2.2", {"start": v(-5.78, 6.09) * mm, "end": v(-6.24, 5.75) * mm});
            skLineSegment(sketch, "E26.5.2.3", {"start": v(-6.24, 5.75) * mm, "end": v(-6.06, 5.2) * mm});
            skLineSegment(sketch, "E26.5.2.4", {"start": v(-6.53, 5.54) * mm, "end": v(-6.06, 5.2) * mm});
            skLineSegment(sketch, "E26.5.2.5", {"start": v(-6.53, 5.54) * mm, "end": v(-7, 5.2) * mm});
            skLineSegment(sketch, "E26.5.2.6", {"start": v(-7, 5.2) * mm, "end": v(-6.81, 5.75) * mm});
            skLineSegment(sketch, "E26.5.2.7", {"start": v(-7.28, 6.09) * mm, "end": v(-6.81, 5.75) * mm});
            skLineSegment(sketch, "E26.5.2.8", {"start": v(-6.7, 6.09) * mm, "end": v(-6.53, 6.63) * mm});
            skLineSegment(sketch, "E26.5.2.9", {"start": v(-6.7, 6.09) * mm, "end": v(-7.28, 6.09) * mm});
            skLineSegment(sketch, "E26.5.3.0", {"start": v(-6.53, 3.89) * mm, "end": v(-6.35, 3.34) * mm});
            skLineSegment(sketch, "E26.5.3.1", {"start": v(-5.78, 3.34) * mm, "end": v(-6.35, 3.34) * mm});
            skLineSegment(sketch, "E26.5.3.2", {"start": v(-5.78, 3.34) * mm, "end": v(-6.24, 3) * mm});
            skLineSegment(sketch, "E26.5.3.3", {"start": v(-6.24, 3) * mm, "end": v(-6.06, 2.46) * mm});
            skLineSegment(sketch, "E26.5.3.4", {"start": v(-6.53, 2.8) * mm, "end": v(-6.06, 2.46) * mm});
            skLineSegment(sketch, "E26.5.3.5", {"start": v(-6.53, 2.8) * mm, "end": v(-7, 2.46) * mm});
            skLineSegment(sketch, "E26.5.3.6", {"start": v(-7, 2.46) * mm, "end": v(-6.81, 3) * mm});
            skLineSegment(sketch, "E26.5.3.7", {"start": v(-7.28, 3.34) * mm, "end": v(-6.81, 3) * mm});
            skLineSegment(sketch, "E26.5.3.8", {"start": v(-6.7, 3.34) * mm, "end": v(-6.53, 3.89) * mm});
            skLineSegment(sketch, "E26.5.3.9", {"start": v(-6.7, 3.34) * mm, "end": v(-7.28, 3.34) * mm});
            skLineSegment(sketch, "E26.5.4.0", {"start": v(-6.53, 1.14) * mm, "end": v(-6.35, 0.6) * mm});
            skLineSegment(sketch, "E26.5.4.1", {"start": v(-5.78, 0.6) * mm, "end": v(-6.35, 0.6) * mm});
            skLineSegment(sketch, "E26.5.4.2", {"start": v(-5.78, 0.6) * mm, "end": v(-6.24, 0.26) * mm});
            skLineSegment(sketch, "E26.5.4.3", {"start": v(-6.24, 0.26) * mm, "end": v(-6.06, -0.28) * mm});
            skLineSegment(sketch, "E26.5.4.4", {"start": v(-6.53, 0.05) * mm, "end": v(-6.06, -0.28) * mm});
            skLineSegment(sketch, "E26.5.4.5", {"start": v(-6.53, 0.05) * mm, "end": v(-7, -0.28) * mm});
            skLineSegment(sketch, "E26.5.4.6", {"start": v(-7, -0.28) * mm, "end": v(-6.81, 0.26) * mm});
            skLineSegment(sketch, "E26.5.4.7", {"start": v(-7.28, 0.6) * mm, "end": v(-6.81, 0.26) * mm});
            skLineSegment(sketch, "E26.5.4.8", {"start": v(-6.7, 0.6) * mm, "end": v(-6.53, 1.14) * mm});
            skLineSegment(sketch, "E26.5.4.9", {"start": v(-6.7, 0.6) * mm, "end": v(-7.28, 0.6) * mm});
            skLineSegment(sketch, "E26.direction1", {"start": v(-22.35, 11.57) * mm, "end": v(-19.15, 11.57) * mm, "construction": true});
            skLineSegment(sketch, "E26.direction2", {"start": v(-22.35, 11.57) * mm, "end": v(-22.35, 8.83) * mm, "construction": true});
            skPoint(sketch, "E27.cCircle.perimeterSnap0", {"position": v(-20.93, 10.64) * mm});
            skPoint(sketch, "E27.0.startSnap0", {"position": v(-20.93, 10.64) * mm});
            skLineSegment(sketch, "E28", {"start": v(-20.93, 10.75) * mm, "end": v(-20.75, 10.2) * mm});
            skLineSegment(sketch, "E29", {"start": v(-21.68, 10.2) * mm, "end": v(-21.1, 10.2) * mm});
            skLineSegment(sketch, "E30", {"start": v(-21.4, 9.32) * mm, "end": v(-20.93, 9.66) * mm});
            skLineSegment(sketch, "E31", {"start": v(-21.4, 9.32) * mm, "end": v(-21.22, 9.86) * mm});
            skLineSegment(sketch, "E32", {"start": v(-20.47, 9.32) * mm, "end": v(-20.93, 9.66) * mm});
            skLineSegment(sketch, "E33.trimOffspring", {"start": v(-20.64, 9.86) * mm, "end": v(-20.47, 9.32) * mm});
            skLineSegment(sketch, "E34.trimOffspring", {"start": v(-20.75, 10.2) * mm, "end": v(-20.18, 10.2) * mm});
            skLineSegment(sketch, "E35.trimOffspring", {"start": v(-21.1, 10.2) * mm, "end": v(-20.93, 10.75) * mm});
            skLineSegment(sketch, "E36.trimOffspring", {"start": v(-21.22, 9.86) * mm, "end": v(-21.68, 10.2) * mm});
            skLineSegment(sketch, "E37.trimOffspring", {"start": v(-20.64, 9.86) * mm, "end": v(-20.18, 10.2) * mm});
            skLineSegment(sketch, "E38.0.1.0", {"start": v(-20.93, 8) * mm, "end": v(-20.75, 7.46) * mm});
            skLineSegment(sketch, "E38.0.1.1", {"start": v(-20.75, 7.46) * mm, "end": v(-20.18, 7.46) * mm});
            skLineSegment(sketch, "E38.0.1.2", {"start": v(-20.64, 7.12) * mm, "end": v(-20.18, 7.46) * mm});
            skLineSegment(sketch, "E38.0.1.3", {"start": v(-20.64, 7.12) * mm, "end": v(-20.47, 6.57) * mm});
            skLineSegment(sketch, "E38.0.1.4", {"start": v(-20.47, 6.57) * mm, "end": v(-20.93, 6.91) * mm});
            skLineSegment(sketch, "E38.0.1.5", {"start": v(-21.4, 6.57) * mm, "end": v(-20.93, 6.91) * mm});
            skLineSegment(sketch, "E38.0.1.6", {"start": v(-21.4, 6.57) * mm, "end": v(-21.22, 7.12) * mm});
            skLineSegment(sketch, "E38.0.1.7", {"start": v(-21.22, 7.12) * mm, "end": v(-21.68, 7.46) * mm});
            skLineSegment(sketch, "E38.0.1.8", {"start": v(-21.68, 7.46) * mm, "end": v(-21.1, 7.46) * mm});
            skLineSegment(sketch, "E38.0.1.9", {"start": v(-21.1, 7.46) * mm, "end": v(-20.93, 8) * mm});
            skLineSegment(sketch, "E38.0.2.0", {"start": v(-20.93, 5.26) * mm, "end": v(-20.75, 4.71) * mm});
            skLineSegment(sketch, "E38.0.2.1", {"start": v(-20.75, 4.71) * mm, "end": v(-20.18, 4.71) * mm});
            skLineSegment(sketch, "E38.0.2.2", {"start": v(-20.64, 4.38) * mm, "end": v(-20.18, 4.71) * mm});
            skLineSegment(sketch, "E38.0.2.3", {"start": v(-20.64, 4.38) * mm, "end": v(-20.47, 3.83) * mm});
            skLineSegment(sketch, "E38.0.2.4", {"start": v(-20.47, 3.83) * mm, "end": v(-20.93, 4.17) * mm});
            skLineSegment(sketch, "E38.0.2.5", {"start": v(-21.4, 3.83) * mm, "end": v(-20.93, 4.17) * mm});
            skLineSegment(sketch, "E38.0.2.6", {"start": v(-21.4, 3.83) * mm, "end": v(-21.22, 4.38) * mm});
            skLineSegment(sketch, "E38.0.2.7", {"start": v(-21.22, 4.38) * mm, "end": v(-21.68, 4.71) * mm});
            skLineSegment(sketch, "E38.0.2.8", {"start": v(-21.68, 4.71) * mm, "end": v(-21.1, 4.71) * mm});
            skLineSegment(sketch, "E38.0.2.9", {"start": v(-21.1, 4.71) * mm, "end": v(-20.93, 5.26) * mm});
            skLineSegment(sketch, "E38.0.3.0", {"start": v(-20.93, 2.52) * mm, "end": v(-20.75, 1.97) * mm});
            skLineSegment(sketch, "E38.0.3.1", {"start": v(-20.75, 1.97) * mm, "end": v(-20.18, 1.97) * mm});
            skLineSegment(sketch, "E38.0.3.2", {"start": v(-20.64, 1.63) * mm, "end": v(-20.18, 1.97) * mm});
            skLineSegment(sketch, "E38.0.3.3", {"start": v(-20.64, 1.63) * mm, "end": v(-20.47, 1.09) * mm});
            skLineSegment(sketch, "E38.0.3.4", {"start": v(-20.47, 1.09) * mm, "end": v(-20.93, 1.43) * mm});
            skLineSegment(sketch, "E38.0.3.5", {"start": v(-21.4, 1.09) * mm, "end": v(-20.93, 1.43) * mm});
            skLineSegment(sketch, "E38.0.3.6", {"start": v(-21.4, 1.09) * mm, "end": v(-21.22, 1.63) * mm});
            skLineSegment(sketch, "E38.0.3.7", {"start": v(-21.22, 1.63) * mm, "end": v(-21.68, 1.97) * mm});
            skLineSegment(sketch, "E38.0.3.8", {"start": v(-21.68, 1.97) * mm, "end": v(-21.1, 1.97) * mm});
            skLineSegment(sketch, "E38.0.3.9", {"start": v(-21.1, 1.97) * mm, "end": v(-20.93, 2.52) * mm});
            skLineSegment(sketch, "E38.1.0.0", {"start": v(-17.73, 10.75) * mm, "end": v(-17.55, 10.2) * mm});
            skLineSegment(sketch, "E38.1.0.1", {"start": v(-17.55, 10.2) * mm, "end": v(-16.98, 10.2) * mm});
            skLineSegment(sketch, "E38.1.0.2", {"start": v(-17.44, 9.86) * mm, "end": v(-16.98, 10.2) * mm});
            skLineSegment(sketch, "E38.1.0.3", {"start": v(-17.44, 9.86) * mm, "end": v(-17.26, 9.32) * mm});
            skLineSegment(sketch, "E38.1.0.4", {"start": v(-17.26, 9.32) * mm, "end": v(-17.73, 9.66) * mm});
            skLineSegment(sketch, "E38.1.0.5", {"start": v(-18.2, 9.32) * mm, "end": v(-17.73, 9.66) * mm});
            skLineSegment(sketch, "E38.1.0.6", {"start": v(-18.2, 9.32) * mm, "end": v(-18.02, 9.86) * mm});
            skLineSegment(sketch, "E38.1.0.7", {"start": v(-18.02, 9.86) * mm, "end": v(-18.48, 10.2) * mm});
            skLineSegment(sketch, "E38.1.0.8", {"start": v(-18.48, 10.2) * mm, "end": v(-17.9, 10.2) * mm});
            skLineSegment(sketch, "E38.1.0.9", {"start": v(-17.9, 10.2) * mm, "end": v(-17.73, 10.75) * mm});
            skLineSegment(sketch, "E38.1.1.0", {"start": v(-17.73, 8) * mm, "end": v(-17.55, 7.46) * mm});
            skLineSegment(sketch, "E38.1.1.1", {"start": v(-17.55, 7.46) * mm, "end": v(-16.98, 7.46) * mm});
            skLineSegment(sketch, "E38.1.1.2", {"start": v(-17.44, 7.12) * mm, "end": v(-16.98, 7.46) * mm});
            skLineSegment(sketch, "E38.1.1.3", {"start": v(-17.44, 7.12) * mm, "end": v(-17.26, 6.57) * mm});
            skLineSegment(sketch, "E38.1.1.4", {"start": v(-17.26, 6.57) * mm, "end": v(-17.73, 6.91) * mm});
            skLineSegment(sketch, "E38.1.1.5", {"start": v(-18.2, 6.57) * mm, "end": v(-17.73, 6.91) * mm});
            skLineSegment(sketch, "E38.1.1.6", {"start": v(-18.2, 6.57) * mm, "end": v(-18.02, 7.12) * mm});
            skLineSegment(sketch, "E38.1.1.7", {"start": v(-18.02, 7.12) * mm, "end": v(-18.48, 7.46) * mm});
            skLineSegment(sketch, "E38.1.1.8", {"start": v(-18.48, 7.46) * mm, "end": v(-17.9, 7.46) * mm});
            skLineSegment(sketch, "E38.1.1.9", {"start": v(-17.9, 7.46) * mm, "end": v(-17.73, 8) * mm});
            skLineSegment(sketch, "E38.1.2.0", {"start": v(-17.73, 5.26) * mm, "end": v(-17.55, 4.71) * mm});
            skLineSegment(sketch, "E38.1.2.1", {"start": v(-17.55, 4.71) * mm, "end": v(-16.98, 4.71) * mm});
            skLineSegment(sketch, "E38.1.2.2", {"start": v(-17.44, 4.38) * mm, "end": v(-16.98, 4.71) * mm});
            skLineSegment(sketch, "E38.1.2.3", {"start": v(-17.44, 4.38) * mm, "end": v(-17.26, 3.83) * mm});
            skLineSegment(sketch, "E38.1.2.4", {"start": v(-17.26, 3.83) * mm, "end": v(-17.73, 4.17) * mm});
            skLineSegment(sketch, "E38.1.2.5", {"start": v(-18.2, 3.83) * mm, "end": v(-17.73, 4.17) * mm});
            skLineSegment(sketch, "E38.1.2.6", {"start": v(-18.2, 3.83) * mm, "end": v(-18.02, 4.38) * mm});
            skLineSegment(sketch, "E38.1.2.7", {"start": v(-18.02, 4.38) * mm, "end": v(-18.48, 4.71) * mm});
            skLineSegment(sketch, "E38.1.2.8", {"start": v(-18.48, 4.71) * mm, "end": v(-17.9, 4.71) * mm});
            skLineSegment(sketch, "E38.1.2.9", {"start": v(-17.9, 4.71) * mm, "end": v(-17.73, 5.26) * mm});
            skLineSegment(sketch, "E38.1.3.0", {"start": v(-17.73, 2.52) * mm, "end": v(-17.55, 1.97) * mm});
            skLineSegment(sketch, "E38.1.3.1", {"start": v(-17.55, 1.97) * mm, "end": v(-16.98, 1.97) * mm});
            skLineSegment(sketch, "E38.1.3.2", {"start": v(-17.44, 1.63) * mm, "end": v(-16.98, 1.97) * mm});
            skLineSegment(sketch, "E38.1.3.3", {"start": v(-17.44, 1.63) * mm, "end": v(-17.26, 1.09) * mm});
            skLineSegment(sketch, "E38.1.3.4", {"start": v(-17.26, 1.09) * mm, "end": v(-17.73, 1.43) * mm});
            skLineSegment(sketch, "E38.1.3.5", {"start": v(-18.2, 1.09) * mm, "end": v(-17.73, 1.43) * mm});
            skLineSegment(sketch, "E38.1.3.6", {"start": v(-18.2, 1.09) * mm, "end": v(-18.02, 1.63) * mm});
            skLineSegment(sketch, "E38.1.3.7", {"start": v(-18.02, 1.63) * mm, "end": v(-18.48, 1.97) * mm});
            skLineSegment(sketch, "E38.1.3.8", {"start": v(-18.48, 1.97) * mm, "end": v(-17.9, 1.97) * mm});
            skLineSegment(sketch, "E38.1.3.9", {"start": v(-17.9, 1.97) * mm, "end": v(-17.73, 2.52) * mm});
            skLineSegment(sketch, "E38.2.0.0", {"start": v(-14.53, 10.75) * mm, "end": v(-14.35, 10.2) * mm});
            skLineSegment(sketch, "E38.2.0.1", {"start": v(-14.35, 10.2) * mm, "end": v(-13.78, 10.2) * mm});
            skLineSegment(sketch, "E38.2.0.2", {"start": v(-14.24, 9.86) * mm, "end": v(-13.78, 10.2) * mm});
            skLineSegment(sketch, "E38.2.0.3", {"start": v(-14.24, 9.86) * mm, "end": v(-14.06, 9.32) * mm});
            skLineSegment(sketch, "E38.2.0.4", {"start": v(-14.06, 9.32) * mm, "end": v(-14.53, 9.66) * mm});
            skLineSegment(sketch, "E38.2.0.5", {"start": v(-15, 9.32) * mm, "end": v(-14.53, 9.66) * mm});
            skLineSegment(sketch, "E38.2.0.6", {"start": v(-15, 9.32) * mm, "end": v(-14.82, 9.86) * mm});
            skLineSegment(sketch, "E38.2.0.7", {"start": v(-14.82, 9.86) * mm, "end": v(-15.28, 10.2) * mm});
            skLineSegment(sketch, "E38.2.0.8", {"start": v(-15.28, 10.2) * mm, "end": v(-14.7, 10.2) * mm});
            skLineSegment(sketch, "E38.2.0.9", {"start": v(-14.7, 10.2) * mm, "end": v(-14.53, 10.75) * mm});
            skLineSegment(sketch, "E38.2.1.0", {"start": v(-14.53, 8) * mm, "end": v(-14.35, 7.46) * mm});
            skLineSegment(sketch, "E38.2.1.1", {"start": v(-14.35, 7.46) * mm, "end": v(-13.78, 7.46) * mm});
            skLineSegment(sketch, "E38.2.1.2", {"start": v(-14.24, 7.12) * mm, "end": v(-13.78, 7.46) * mm});
            skLineSegment(sketch, "E38.2.1.3", {"start": v(-14.24, 7.12) * mm, "end": v(-14.06, 6.57) * mm});
            skLineSegment(sketch, "E38.2.1.4", {"start": v(-14.06, 6.57) * mm, "end": v(-14.53, 6.91) * mm});
            skLineSegment(sketch, "E38.2.1.5", {"start": v(-15, 6.57) * mm, "end": v(-14.53, 6.91) * mm});
            skLineSegment(sketch, "E38.2.1.6", {"start": v(-15, 6.57) * mm, "end": v(-14.82, 7.12) * mm});
            skLineSegment(sketch, "E38.2.1.7", {"start": v(-14.82, 7.12) * mm, "end": v(-15.28, 7.46) * mm});
            skLineSegment(sketch, "E38.2.1.8", {"start": v(-15.28, 7.46) * mm, "end": v(-14.7, 7.46) * mm});
            skLineSegment(sketch, "E38.2.1.9", {"start": v(-14.7, 7.46) * mm, "end": v(-14.53, 8) * mm});
            skLineSegment(sketch, "E38.2.2.0", {"start": v(-14.53, 5.26) * mm, "end": v(-14.35, 4.71) * mm});
            skLineSegment(sketch, "E38.2.2.1", {"start": v(-14.35, 4.71) * mm, "end": v(-13.78, 4.71) * mm});
            skLineSegment(sketch, "E38.2.2.2", {"start": v(-14.24, 4.38) * mm, "end": v(-13.78, 4.71) * mm});
            skLineSegment(sketch, "E38.2.2.3", {"start": v(-14.24, 4.38) * mm, "end": v(-14.06, 3.83) * mm});
            skLineSegment(sketch, "E38.2.2.4", {"start": v(-14.06, 3.83) * mm, "end": v(-14.53, 4.17) * mm});
            skLineSegment(sketch, "E38.2.2.5", {"start": v(-15, 3.83) * mm, "end": v(-14.53, 4.17) * mm});
            skLineSegment(sketch, "E38.2.2.6", {"start": v(-15, 3.83) * mm, "end": v(-14.82, 4.38) * mm});
            skLineSegment(sketch, "E38.2.2.7", {"start": v(-14.82, 4.38) * mm, "end": v(-15.28, 4.71) * mm});
            skLineSegment(sketch, "E38.2.2.8", {"start": v(-15.28, 4.71) * mm, "end": v(-14.7, 4.71) * mm});
            skLineSegment(sketch, "E38.2.2.9", {"start": v(-14.7, 4.71) * mm, "end": v(-14.53, 5.26) * mm});
            skLineSegment(sketch, "E38.2.3.0", {"start": v(-14.53, 2.52) * mm, "end": v(-14.35, 1.97) * mm});
            skLineSegment(sketch, "E38.2.3.1", {"start": v(-14.35, 1.97) * mm, "end": v(-13.78, 1.97) * mm});
            skLineSegment(sketch, "E38.2.3.2", {"start": v(-14.24, 1.63) * mm, "end": v(-13.78, 1.97) * mm});
            skLineSegment(sketch, "E38.2.3.3", {"start": v(-14.24, 1.63) * mm, "end": v(-14.06, 1.09) * mm});
            skLineSegment(sketch, "E38.2.3.4", {"start": v(-14.06, 1.09) * mm, "end": v(-14.53, 1.43) * mm});
            skLineSegment(sketch, "E38.2.3.5", {"start": v(-15, 1.09) * mm, "end": v(-14.53, 1.43) * mm});
            skLineSegment(sketch, "E38.2.3.6", {"start": v(-15, 1.09) * mm, "end": v(-14.82, 1.63) * mm});
            skLineSegment(sketch, "E38.2.3.7", {"start": v(-14.82, 1.63) * mm, "end": v(-15.28, 1.97) * mm});
            skLineSegment(sketch, "E38.2.3.8", {"start": v(-15.28, 1.97) * mm, "end": v(-14.7, 1.97) * mm});
            skLineSegment(sketch, "E38.2.3.9", {"start": v(-14.7, 1.97) * mm, "end": v(-14.53, 2.52) * mm});
            skLineSegment(sketch, "E38.3.0.0", {"start": v(-11.33, 10.75) * mm, "end": v(-11.15, 10.2) * mm});
            skLineSegment(sketch, "E38.3.0.1", {"start": v(-11.15, 10.2) * mm, "end": v(-10.58, 10.2) * mm});
            skLineSegment(sketch, "E38.3.0.2", {"start": v(-11.04, 9.86) * mm, "end": v(-10.58, 10.2) * mm});
            skLineSegment(sketch, "E38.3.0.3", {"start": v(-11.04, 9.86) * mm, "end": v(-10.86, 9.32) * mm});
            skLineSegment(sketch, "E38.3.0.4", {"start": v(-10.86, 9.32) * mm, "end": v(-11.33, 9.66) * mm});
            skLineSegment(sketch, "E38.3.0.5", {"start": v(-11.8, 9.32) * mm, "end": v(-11.33, 9.66) * mm});
            skLineSegment(sketch, "E38.3.0.6", {"start": v(-11.8, 9.32) * mm, "end": v(-11.62, 9.86) * mm});
            skLineSegment(sketch, "E38.3.0.7", {"start": v(-11.62, 9.86) * mm, "end": v(-12.08, 10.2) * mm});
            skLineSegment(sketch, "E38.3.0.8", {"start": v(-12.08, 10.2) * mm, "end": v(-11.5, 10.2) * mm});
            skLineSegment(sketch, "E38.3.0.9", {"start": v(-11.5, 10.2) * mm, "end": v(-11.33, 10.75) * mm});
            skLineSegment(sketch, "E38.3.1.0", {"start": v(-11.33, 8) * mm, "end": v(-11.15, 7.46) * mm});
            skLineSegment(sketch, "E38.3.1.1", {"start": v(-11.15, 7.46) * mm, "end": v(-10.58, 7.46) * mm});
            skLineSegment(sketch, "E38.3.1.2", {"start": v(-11.04, 7.12) * mm, "end": v(-10.58, 7.46) * mm});
            skLineSegment(sketch, "E38.3.1.3", {"start": v(-11.04, 7.12) * mm, "end": v(-10.86, 6.57) * mm});
            skLineSegment(sketch, "E38.3.1.4", {"start": v(-10.86, 6.57) * mm, "end": v(-11.33, 6.91) * mm});
            skLineSegment(sketch, "E38.3.1.5", {"start": v(-11.8, 6.57) * mm, "end": v(-11.33, 6.91) * mm});
            skLineSegment(sketch, "E38.3.1.6", {"start": v(-11.8, 6.57) * mm, "end": v(-11.62, 7.12) * mm});
            skLineSegment(sketch, "E38.3.1.7", {"start": v(-11.62, 7.12) * mm, "end": v(-12.08, 7.46) * mm});
            skLineSegment(sketch, "E38.3.1.8", {"start": v(-12.08, 7.46) * mm, "end": v(-11.5, 7.46) * mm});
            skLineSegment(sketch, "E38.3.1.9", {"start": v(-11.5, 7.46) * mm, "end": v(-11.33, 8) * mm});
            skLineSegment(sketch, "E38.3.2.0", {"start": v(-11.33, 5.26) * mm, "end": v(-11.15, 4.71) * mm});
            skLineSegment(sketch, "E38.3.2.1", {"start": v(-11.15, 4.71) * mm, "end": v(-10.58, 4.71) * mm});
            skLineSegment(sketch, "E38.3.2.2", {"start": v(-11.04, 4.38) * mm, "end": v(-10.58, 4.71) * mm});
            skLineSegment(sketch, "E38.3.2.3", {"start": v(-11.04, 4.38) * mm, "end": v(-10.86, 3.83) * mm});
            skLineSegment(sketch, "E38.3.2.4", {"start": v(-10.86, 3.83) * mm, "end": v(-11.33, 4.17) * mm});
            skLineSegment(sketch, "E38.3.2.5", {"start": v(-11.8, 3.83) * mm, "end": v(-11.33, 4.17) * mm});
            skLineSegment(sketch, "E38.3.2.6", {"start": v(-11.8, 3.83) * mm, "end": v(-11.62, 4.38) * mm});
            skLineSegment(sketch, "E38.3.2.7", {"start": v(-11.62, 4.38) * mm, "end": v(-12.08, 4.71) * mm});
            skLineSegment(sketch, "E38.3.2.8", {"start": v(-12.08, 4.71) * mm, "end": v(-11.5, 4.71) * mm});
            skLineSegment(sketch, "E38.3.2.9", {"start": v(-11.5, 4.71) * mm, "end": v(-11.33, 5.26) * mm});
            skLineSegment(sketch, "E38.3.3.0", {"start": v(-11.33, 2.52) * mm, "end": v(-11.15, 1.97) * mm});
            skLineSegment(sketch, "E38.3.3.1", {"start": v(-11.15, 1.97) * mm, "end": v(-10.58, 1.97) * mm});
            skLineSegment(sketch, "E38.3.3.2", {"start": v(-11.04, 1.63) * mm, "end": v(-10.58, 1.97) * mm});
            skLineSegment(sketch, "E38.3.3.3", {"start": v(-11.04, 1.63) * mm, "end": v(-10.86, 1.09) * mm});
            skLineSegment(sketch, "E38.3.3.4", {"start": v(-10.86, 1.09) * mm, "end": v(-11.33, 1.43) * mm});
            skLineSegment(sketch, "E38.3.3.5", {"start": v(-11.8, 1.09) * mm, "end": v(-11.33, 1.43) * mm});
            skLineSegment(sketch, "E38.3.3.6", {"start": v(-11.8, 1.09) * mm, "end": v(-11.62, 1.63) * mm});
            skLineSegment(sketch, "E38.3.3.7", {"start": v(-11.62, 1.63) * mm, "end": v(-12.08, 1.97) * mm});
            skLineSegment(sketch, "E38.3.3.8", {"start": v(-12.08, 1.97) * mm, "end": v(-11.5, 1.97) * mm});
            skLineSegment(sketch, "E38.3.3.9", {"start": v(-11.5, 1.97) * mm, "end": v(-11.33, 2.52) * mm});
            skLineSegment(sketch, "E38.4.0.0", {"start": v(-8.13, 10.75) * mm, "end": v(-7.95, 10.2) * mm});
            skLineSegment(sketch, "E38.4.0.1", {"start": v(-7.95, 10.2) * mm, "end": v(-7.38, 10.2) * mm});
            skLineSegment(sketch, "E38.4.0.2", {"start": v(-7.84, 9.86) * mm, "end": v(-7.38, 10.2) * mm});
            skLineSegment(sketch, "E38.4.0.3", {"start": v(-7.84, 9.86) * mm, "end": v(-7.66, 9.32) * mm});
            skLineSegment(sketch, "E38.4.0.4", {"start": v(-7.66, 9.32) * mm, "end": v(-8.13, 9.66) * mm});
            skLineSegment(sketch, "E38.4.0.5", {"start": v(-8.6, 9.32) * mm, "end": v(-8.13, 9.66) * mm});
            skLineSegment(sketch, "E38.4.0.6", {"start": v(-8.6, 9.32) * mm, "end": v(-8.41, 9.86) * mm});
            skLineSegment(sketch, "E38.4.0.7", {"start": v(-8.41, 9.86) * mm, "end": v(-8.88, 10.2) * mm});
            skLineSegment(sketch, "E38.4.0.8", {"start": v(-8.88, 10.2) * mm, "end": v(-8.3, 10.2) * mm});
            skLineSegment(sketch, "E38.4.0.9", {"start": v(-8.3, 10.2) * mm, "end": v(-8.13, 10.75) * mm});
            skLineSegment(sketch, "E38.4.1.0", {"start": v(-8.13, 8) * mm, "end": v(-7.95, 7.46) * mm});
            skLineSegment(sketch, "E38.4.1.1", {"start": v(-7.95, 7.46) * mm, "end": v(-7.38, 7.46) * mm});
            skLineSegment(sketch, "E38.4.1.2", {"start": v(-7.84, 7.12) * mm, "end": v(-7.38, 7.46) * mm});
            skLineSegment(sketch, "E38.4.1.3", {"start": v(-7.84, 7.12) * mm, "end": v(-7.66, 6.57) * mm});
            skLineSegment(sketch, "E38.4.1.4", {"start": v(-7.66, 6.57) * mm, "end": v(-8.13, 6.91) * mm});
            skLineSegment(sketch, "E38.4.1.5", {"start": v(-8.6, 6.57) * mm, "end": v(-8.13, 6.91) * mm});
            skLineSegment(sketch, "E38.4.1.6", {"start": v(-8.6, 6.57) * mm, "end": v(-8.41, 7.12) * mm});
            skLineSegment(sketch, "E38.4.1.7", {"start": v(-8.41, 7.12) * mm, "end": v(-8.88, 7.46) * mm});
            skLineSegment(sketch, "E38.4.1.8", {"start": v(-8.88, 7.46) * mm, "end": v(-8.3, 7.46) * mm});
            skLineSegment(sketch, "E38.4.1.9", {"start": v(-8.3, 7.46) * mm, "end": v(-8.13, 8) * mm});
            skLineSegment(sketch, "E38.4.2.0", {"start": v(-8.13, 5.26) * mm, "end": v(-7.95, 4.71) * mm});
            skLineSegment(sketch, "E38.4.2.1", {"start": v(-7.95, 4.71) * mm, "end": v(-7.38, 4.71) * mm});
            skLineSegment(sketch, "E38.4.2.2", {"start": v(-7.84, 4.38) * mm, "end": v(-7.38, 4.71) * mm});
            skLineSegment(sketch, "E38.4.2.3", {"start": v(-7.84, 4.38) * mm, "end": v(-7.66, 3.83) * mm});
            skLineSegment(sketch, "E38.4.2.4", {"start": v(-7.66, 3.83) * mm, "end": v(-8.13, 4.17) * mm});
            skLineSegment(sketch, "E38.4.2.5", {"start": v(-8.6, 3.83) * mm, "end": v(-8.13, 4.17) * mm});
            skLineSegment(sketch, "E38.4.2.6", {"start": v(-8.6, 3.83) * mm, "end": v(-8.41, 4.38) * mm});
            skLineSegment(sketch, "E38.4.2.7", {"start": v(-8.41, 4.38) * mm, "end": v(-8.88, 4.71) * mm});
            skLineSegment(sketch, "E38.4.2.8", {"start": v(-8.88, 4.71) * mm, "end": v(-8.3, 4.71) * mm});
            skLineSegment(sketch, "E38.4.2.9", {"start": v(-8.3, 4.71) * mm, "end": v(-8.13, 5.26) * mm});
            skLineSegment(sketch, "E38.4.3.0", {"start": v(-8.13, 2.52) * mm, "end": v(-7.95, 1.97) * mm});
            skLineSegment(sketch, "E38.4.3.1", {"start": v(-7.95, 1.97) * mm, "end": v(-7.38, 1.97) * mm});
            skLineSegment(sketch, "E38.4.3.2", {"start": v(-7.84, 1.63) * mm, "end": v(-7.38, 1.97) * mm});
            skLineSegment(sketch, "E38.4.3.3", {"start": v(-7.84, 1.63) * mm, "end": v(-7.66, 1.09) * mm});
            skLineSegment(sketch, "E38.4.3.4", {"start": v(-7.66, 1.09) * mm, "end": v(-8.13, 1.43) * mm});
            skLineSegment(sketch, "E38.4.3.5", {"start": v(-8.6, 1.09) * mm, "end": v(-8.13, 1.43) * mm});
            skLineSegment(sketch, "E38.4.3.6", {"start": v(-8.6, 1.09) * mm, "end": v(-8.41, 1.63) * mm});
            skLineSegment(sketch, "E38.4.3.7", {"start": v(-8.41, 1.63) * mm, "end": v(-8.88, 1.97) * mm});
            skLineSegment(sketch, "E38.4.3.8", {"start": v(-8.88, 1.97) * mm, "end": v(-8.3, 1.97) * mm});
            skLineSegment(sketch, "E38.4.3.9", {"start": v(-8.3, 1.97) * mm, "end": v(-8.13, 2.52) * mm});
            skLineSegment(sketch, "E38.direction1", {"start": v(-20.75, 10.2) * mm, "end": v(-17.55, 10.2) * mm, "construction": true});
            skLineSegment(sketch, "E38.direction2", {"start": v(-20.75, 10.2) * mm, "end": v(-20.75, 7.46) * mm, "construction": true});
            skSolve(sketch);
        }
        {
            var Q0;
            Q0=makeQuery(id+"F0.imprint","IMPRINT",FACE,{"disambiguationData":[TD([[makeQuery(id+"F0.imprint","IMPRINT",EDGE,{"derivedFrom":sQuery(id+"F0.wireOp",EDGE,"E16")}),-1.0]])]});
            var Q1;
            Q1=makeQuery(id+"F0.imprint","IMPRINT",FACE,{"disambiguationData":[TD([[makeQuery(id+"F0.imprint","IMPRINT",EDGE,{"derivedFrom":sQuery(id+"F0.wireOp",EDGE,"E26.0.1.0")}),-1.0]])]});
            var Q2;
            Q2=makeQuery(id+"F0.imprint","IMPRINT",FACE,{"disambiguationData":[TD([[makeQuery(id+"F0.imprint","IMPRINT",EDGE,{"derivedFrom":sQuery(id+"F0.wireOp",EDGE,"E28")}),-1.0]])]});
            var Q3;
            Q3=makeQuery(id+"F0.imprint","IMPRINT",FACE,{"disambiguationData":[TD([[makeQuery(id+"F0.imprint","IMPRINT",EDGE,{"derivedFrom":sQuery(id+"F0.wireOp",EDGE,"E26.1.0.0")}),-1.0]])]});
            var Q4;
            Q4=makeQuery(id+"F0.imprint","IMPRINT",FACE,{"disambiguationData":[TD([[makeQuery(id+"F0.imprint","IMPRINT",EDGE,{"derivedFrom":sQuery(id+"F0.wireOp",EDGE,"E26.2.0.0")}),-1.0]])]});
            var Q5;
            Q5=makeQuery(id+"F0.imprint","IMPRINT",FACE,{"disambiguationData":[TD([[makeQuery(id+"F0.imprint","IMPRINT",EDGE,{"derivedFrom":sQuery(id+"F0.wireOp",EDGE,"E26.0.2.0")}),-1.0]])]});
            var Q6;
            Q6=makeQuery(id+"F0.imprint","IMPRINT",FACE,{"disambiguationData":[TD([[makeQuery(id+"F0.imprint","IMPRINT",EDGE,{"derivedFrom":sQuery(id+"F0.wireOp",EDGE,"E38.0.1.0")}),-1.0]])]});
            var Q7;
            Q7=makeQuery(id+"F0.imprint","IMPRINT",FACE,{"disambiguationData":[TD([[makeQuery(id+"F0.imprint","IMPRINT",EDGE,{"derivedFrom":sQuery(id+"F0.wireOp",EDGE,"E26.1.1.0")}),-1.0]])]});
            var Q8;
            Q8=makeQuery(id+"F0.imprint","IMPRINT",FACE,{"disambiguationData":[TD([[makeQuery(id+"F0.imprint","IMPRINT",EDGE,{"derivedFrom":sQuery(id+"F0.wireOp",EDGE,"E38.1.0.0")}),-1.0]])]});
            var Q9;
            Q9=makeQuery(id+"F0.imprint","IMPRINT",FACE,{"disambiguationData":[TD([[makeQuery(id+"F0.imprint","IMPRINT",EDGE,{"derivedFrom":sQuery(id+"F0.wireOp",EDGE,"E26.3.0.0")}),-1.0]])]});
            var Q10;
            Q10=makeQuery(id+"F0.imprint","IMPRINT",FACE,{"disambiguationData":[TD([[makeQuery(id+"F0.imprint","IMPRINT",EDGE,{"derivedFrom":sQuery(id+"F0.wireOp",EDGE,"E38.2.0.0")}),-1.0]])]});
            var Q11;
            Q11=makeQuery(id+"F0.imprint","IMPRINT",FACE,{"disambiguationData":[TD([[makeQuery(id+"F0.imprint","IMPRINT",EDGE,{"derivedFrom":sQuery(id+"F0.wireOp",EDGE,"E26.2.1.0")}),-1.0]])]});
            var Q12;
            Q12=makeQuery(id+"F0.imprint","IMPRINT",FACE,{"disambiguationData":[TD([[makeQuery(id+"F0.imprint","IMPRINT",EDGE,{"derivedFrom":sQuery(id+"F0.wireOp",EDGE,"E38.1.1.0")}),-1.0]])]});
            var Q13;
            Q13=makeQuery(id+"F0.imprint","IMPRINT",FACE,{"disambiguationData":[TD([[makeQuery(id+"F0.imprint","IMPRINT",EDGE,{"derivedFrom":sQuery(id+"F0.wireOp",EDGE,"E26.1.2.0")}),-1.0]])]});
            var Q14;
            Q14=makeQuery(id+"F0.imprint","IMPRINT",FACE,{"disambiguationData":[TD([[makeQuery(id+"F0.imprint","IMPRINT",EDGE,{"derivedFrom":sQuery(id+"F0.wireOp",EDGE,"E38.0.2.0")}),-1.0]])]});
            var Q15;
            Q15=makeQuery(id+"F0.imprint","IMPRINT",FACE,{"disambiguationData":[TD([[makeQuery(id+"F0.imprint","IMPRINT",EDGE,{"derivedFrom":sQuery(id+"F0.wireOp",EDGE,"E26.0.3.0")}),-1.0]])]});
            var Q16;
            Q16=makeQuery(id+"F0.imprint","IMPRINT",FACE,{"disambiguationData":[TD([[makeQuery(id+"F0.imprint","IMPRINT",EDGE,{"derivedFrom":sQuery(id+"F0.wireOp",EDGE,"E26.0.4.0")}),-1.0]])]});
            var Q17;
            Q17=makeQuery(id+"F0.imprint","IMPRINT",FACE,{"disambiguationData":[TD([[makeQuery(id+"F0.imprint","IMPRINT",EDGE,{"derivedFrom":sQuery(id+"F0.wireOp",EDGE,"E38.0.3.0")}),-1.0]])]});
            var Q18;
            Q18=makeQuery(id+"F0.imprint","IMPRINT",FACE,{"disambiguationData":[TD([[makeQuery(id+"F0.imprint","IMPRINT",EDGE,{"derivedFrom":sQuery(id+"F0.wireOp",EDGE,"E26.1.3.0")}),-1.0]])]});
            var Q19;
            Q19=makeQuery(id+"F0.imprint","IMPRINT",FACE,{"disambiguationData":[TD([[makeQuery(id+"F0.imprint","IMPRINT",EDGE,{"derivedFrom":sQuery(id+"F0.wireOp",EDGE,"E38.1.2.0")}),-1.0]])]});
            var Q20;
            Q20=makeQuery(id+"F0.imprint","IMPRINT",FACE,{"disambiguationData":[TD([[makeQuery(id+"F0.imprint","IMPRINT",EDGE,{"derivedFrom":sQuery(id+"F0.wireOp",EDGE,"E26.2.2.0")}),-1.0]])]});
            var Q21;
            Q21=makeQuery(id+"F0.imprint","IMPRINT",FACE,{"disambiguationData":[TD([[makeQuery(id+"F0.imprint","IMPRINT",EDGE,{"derivedFrom":sQuery(id+"F0.wireOp",EDGE,"E38.2.1.0")}),-1.0]])]});
            var Q22;
            Q22=makeQuery(id+"F0.imprint","IMPRINT",FACE,{"disambiguationData":[TD([[makeQuery(id+"F0.imprint","IMPRINT",EDGE,{"derivedFrom":sQuery(id+"F0.wireOp",EDGE,"E26.3.1.0")}),-1.0]])]});
            var Q23;
            Q23=makeQuery(id+"F0.imprint","IMPRINT",FACE,{"disambiguationData":[TD([[makeQuery(id+"F0.imprint","IMPRINT",EDGE,{"derivedFrom":sQuery(id+"F0.wireOp",EDGE,"E38.3.0.0")}),-1.0]])]});
            var Q24;
            Q24=makeQuery(id+"F0.imprint","IMPRINT",FACE,{"disambiguationData":[TD([[makeQuery(id+"F0.imprint","IMPRINT",EDGE,{"derivedFrom":sQuery(id+"F0.wireOp",EDGE,"E26.4.0.0")}),-1.0]])]});
            var Q25;
            Q25=makeQuery(id+"F0.imprint","IMPRINT",FACE,{"disambiguationData":[TD([[makeQuery(id+"F0.imprint","IMPRINT",EDGE,{"derivedFrom":sQuery(id+"F0.wireOp",EDGE,"E26.5.0.0")}),-1.0]])]});
            var Q26;
            Q26=makeQuery(id+"F0.imprint","IMPRINT",FACE,{"disambiguationData":[TD([[makeQuery(id+"F0.imprint","IMPRINT",EDGE,{"derivedFrom":sQuery(id+"F0.wireOp",EDGE,"E38.4.0.0")}),-1.0]])]});
            var Q27;
            Q27=makeQuery(id+"F0.imprint","IMPRINT",FACE,{"disambiguationData":[TD([[makeQuery(id+"F0.imprint","IMPRINT",EDGE,{"derivedFrom":sQuery(id+"F0.wireOp",EDGE,"E26.4.1.0")}),-1.0]])]});
            var Q28;
            Q28=makeQuery(id+"F0.imprint","IMPRINT",FACE,{"disambiguationData":[TD([[makeQuery(id+"F0.imprint","IMPRINT",EDGE,{"derivedFrom":sQuery(id+"F0.wireOp",EDGE,"E38.3.1.0")}),-1.0]])]});
            var Q29;
            Q29=makeQuery(id+"F0.imprint","IMPRINT",FACE,{"disambiguationData":[TD([[makeQuery(id+"F0.imprint","IMPRINT",EDGE,{"derivedFrom":sQuery(id+"F0.wireOp",EDGE,"E26.3.2.0")}),-1.0]])]});
            var Q30;
            Q30=makeQuery(id+"F0.imprint","IMPRINT",FACE,{"disambiguationData":[TD([[makeQuery(id+"F0.imprint","IMPRINT",EDGE,{"derivedFrom":sQuery(id+"F0.wireOp",EDGE,"E38.2.2.0")}),-1.0]])]});
            var Q31;
            Q31=makeQuery(id+"F0.imprint","IMPRINT",FACE,{"disambiguationData":[TD([[makeQuery(id+"F0.imprint","IMPRINT",EDGE,{"derivedFrom":sQuery(id+"F0.wireOp",EDGE,"E26.2.3.0")}),-1.0]])]});
            var Q32;
            Q32=makeQuery(id+"F0.imprint","IMPRINT",FACE,{"disambiguationData":[TD([[makeQuery(id+"F0.imprint","IMPRINT",EDGE,{"derivedFrom":sQuery(id+"F0.wireOp",EDGE,"E38.1.3.0")}),-1.0]])]});
            var Q33;
            Q33=makeQuery(id+"F0.imprint","IMPRINT",FACE,{"disambiguationData":[TD([[makeQuery(id+"F0.imprint","IMPRINT",EDGE,{"derivedFrom":sQuery(id+"F0.wireOp",EDGE,"E26.1.4.0")}),-1.0]])]});
            var Q34;
            Q34=makeQuery(id+"F0.imprint","IMPRINT",FACE,{"disambiguationData":[TD([[makeQuery(id+"F0.imprint","IMPRINT",EDGE,{"derivedFrom":sQuery(id+"F0.wireOp",EDGE,"E26.2.4.0")}),-1.0]])]});
            var Q35;
            Q35=makeQuery(id+"F0.imprint","IMPRINT",FACE,{"disambiguationData":[TD([[makeQuery(id+"F0.imprint","IMPRINT",EDGE,{"derivedFrom":sQuery(id+"F0.wireOp",EDGE,"E38.2.3.0")}),-1.0]])]});
            var Q36;
            Q36=makeQuery(id+"F0.imprint","IMPRINT",FACE,{"disambiguationData":[TD([[makeQuery(id+"F0.imprint","IMPRINT",EDGE,{"derivedFrom":sQuery(id+"F0.wireOp",EDGE,"E26.3.3.0")}),-1.0]])]});
            var Q37;
            Q37=makeQuery(id+"F0.imprint","IMPRINT",FACE,{"disambiguationData":[TD([[makeQuery(id+"F0.imprint","IMPRINT",EDGE,{"derivedFrom":sQuery(id+"F0.wireOp",EDGE,"E38.3.2.0")}),-1.0]])]});
            var Q38;
            Q38=makeQuery(id+"F0.imprint","IMPRINT",FACE,{"disambiguationData":[TD([[makeQuery(id+"F0.imprint","IMPRINT",EDGE,{"derivedFrom":sQuery(id+"F0.wireOp",EDGE,"E26.4.2.0")}),-1.0]])]});
            var Q39;
            Q39=makeQuery(id+"F0.imprint","IMPRINT",FACE,{"disambiguationData":[TD([[makeQuery(id+"F0.imprint","IMPRINT",EDGE,{"derivedFrom":sQuery(id+"F0.wireOp",EDGE,"E38.4.1.0")}),-1.0]])]});
            var Q40;
            Q40=makeQuery(id+"F0.imprint","IMPRINT",FACE,{"disambiguationData":[TD([[makeQuery(id+"F0.imprint","IMPRINT",EDGE,{"derivedFrom":sQuery(id+"F0.wireOp",EDGE,"E38.4.2.0")}),-1.0]])]});
            var Q41;
            Q41=makeQuery(id+"F0.imprint","IMPRINT",FACE,{"disambiguationData":[TD([[makeQuery(id+"F0.imprint","IMPRINT",EDGE,{"derivedFrom":sQuery(id+"F0.wireOp",EDGE,"E26.4.3.0")}),-1.0]])]});
            var Q42;
            Q42=makeQuery(id+"F0.imprint","IMPRINT",FACE,{"disambiguationData":[TD([[makeQuery(id+"F0.imprint","IMPRINT",EDGE,{"derivedFrom":sQuery(id+"F0.wireOp",EDGE,"E38.3.3.0")}),-1.0]])]});
            var Q43;
            Q43=makeQuery(id+"F0.imprint","IMPRINT",FACE,{"disambiguationData":[TD([[makeQuery(id+"F0.imprint","IMPRINT",EDGE,{"derivedFrom":sQuery(id+"F0.wireOp",EDGE,"E26.3.4.0")}),-1.0]])]});
            var Q44;
            Q44=makeQuery(id+"F0.imprint","IMPRINT",FACE,{"disambiguationData":[TD([[makeQuery(id+"F0.imprint","IMPRINT",EDGE,{"derivedFrom":sQuery(id+"F0.wireOp",EDGE,"E38.4.3.0")}),-1.0]])]});
            var Q45;
            Q45=makeQuery(id+"F0.imprint","IMPRINT",FACE,{"disambiguationData":[TD([[makeQuery(id+"F0.imprint","IMPRINT",EDGE,{"derivedFrom":sQuery(id+"F0.wireOp",EDGE,"E26.5.3.0")}),-1.0]])]});
            var Q46;
            Q46=makeQuery(id+"F0.imprint","IMPRINT",FACE,{"disambiguationData":[TD([[makeQuery(id+"F0.imprint","IMPRINT",EDGE,{"derivedFrom":sQuery(id+"F0.wireOp",EDGE,"E26.5.4.0")}),-1.0]])]});
            var Q47;
            Q47=makeQuery(id+"F0.imprint","IMPRINT",FACE,{"disambiguationData":[TD([[makeQuery(id+"F0.imprint","IMPRINT",EDGE,{"derivedFrom":sQuery(id+"F0.wireOp",EDGE,"E26.4.4.0")}),-1.0]])]});
            var Q48;
            Q48=makeQuery(id+"F0.imprint","IMPRINT",FACE,{"disambiguationData":[TD([[makeQuery(id+"F0.imprint","IMPRINT",EDGE,{"derivedFrom":sQuery(id+"F0.wireOp",EDGE,"E26.5.2.0")}),-1.0]])]});
            var Q49;
            Q49=makeQuery(id+"F0.imprint","IMPRINT",FACE,{"disambiguationData":[TD([[makeQuery(id+"F0.imprint","IMPRINT",EDGE,{"derivedFrom":sQuery(id+"F0.wireOp",EDGE,"E26.5.1.0")}),-1.0]])]});
            var Q50;
            {var subQ0=sQuery(id+"F0.wireOp",EDGE,"E2.top");Q50=makeQuery(id+"F0.imprint","IMPRINT",FACE,{"disambiguationData":[TD([[makeQuery(id+"F0.imprint","IMPRINT",EDGE,{"derivedFrom":subQ0}),-1.0]])]});}
            var Q51;
            {var subQ0=sQuery(id+"F0.wireOp",EDGE,"E4.MirrorCS");Q51=makeQuery(id+"F0.imprint","IMPRINT",FACE,{"disambiguationData":[TD([[makeQuery(id+"F0.imprint","IMPRINT",EDGE,{"derivedFrom":subQ0}),-1.0]])]});}
            var Q52;
            {var subQ0=sQuery(id+"F0.wireOp",EDGE,"E6.MirrorCS");Q52=makeQuery(id+"F0.imprint","IMPRINT",FACE,{"disambiguationData":[TD([[makeQuery(id+"F0.imprint","IMPRINT",EDGE,{"derivedFrom":subQ0}),-1.0]])]});}
            var Q53;
            Q53=makeQuery(id+"F0.imprint","IMPRINT",FACE,{"disambiguationData":[TD([[makeQuery(id+"F0.imprint","IMPRINT",EDGE,{"derivedFrom":sQuery(id+"F0.wireOp",EDGE,"E9.top")}),1.0]])]});
            var Q54;
            {var subQ0=sQuery(id+"F0.wireOp",EDGE,"E10.MirrorCS");Q54=makeQuery(id+"F0.imprint","IMPRINT",FACE,{"disambiguationData":[TD([[makeQuery(id+"F0.imprint","IMPRINT",EDGE,{"derivedFrom":subQ0}),-1.0]])]});}
            var Q55;
            {var subQ0=sQuery(id+"F0.wireOp",EDGE,"E12.MirrorCS");Q55=makeQuery(id+"F0.imprint","IMPRINT",FACE,{"disambiguationData":[TD([[makeQuery(id+"F0.imprint","IMPRINT",EDGE,{"derivedFrom":subQ0}),-1.0]])]});}
            extrude(context, id + "F1", {"entities" : qUnion([Q0, Q1, Q2, Q3, Q4, Q5, Q6, Q7, Q8, Q9, Q10, Q11, Q12, Q13, Q14, Q15, Q16, Q17, Q18, Q19, Q20, Q21, Q22, Q23, Q24, Q25, Q26, Q27, Q28, Q29, Q30, Q31, Q32, Q33, Q34, Q35, Q36, Q37, Q38, Q39, Q40, Q41, Q42, Q43, Q44, Q45, Q46, Q47, Q48, Q49, Q50, Q51, Q52, Q53, Q54, Q55]), "depth" : 2 * mm, "offsetDistance" : 25.4 * mm});
        }
        {
            var Q0;
            Q0=qCreatedBy(makeId("Top.planeOp"),FACE);
            var sketch = newSketch(context, id + "F2", { "sketchPlane" : qUnion([Q0])});
            skLineSegment(sketch, "E39.bottom", {"start": v(28.58, 15.88) * mm, "end": v(-28.57, 15.88) * mm});
            skLineSegment(sketch, "E39.top", {"start": v(28.57, -15.88) * mm, "end": v(-28.58, -15.88) * mm});
            skLineSegment(sketch, "E39.left", {"start": v(28.58, 15.88) * mm, "end": v(28.57, -15.87) * mm});
            skLineSegment(sketch, "E39.right", {"start": v(-28.57, 15.88) * mm, "end": v(-28.58, -15.88) * mm});
            skPoint(sketch, "E39.middle", {"position": v(0, 0) * mm});
            skLineSegment(sketch, "E40.0", {"start": v(28.83, 16.13) * mm, "end": v(-28.83, 16.13) * mm});
            skLineSegment(sketch, "E40.1", {"start": v(28.83, 16.13) * mm, "end": v(28.83, -16.13) * mm});
            skLineSegment(sketch, "E40.2", {"start": v(28.83, -16.13) * mm, "end": v(-28.83, -16.13) * mm});
            skLineSegment(sketch, "E40.3", {"start": v(-28.83, 16.13) * mm, "end": v(-28.83, -16.13) * mm});
            skSolve(sketch);
        }
        {
            var Q0;
            Q0 = qSketchRegion(id + "F2", true);
            extrude(context, id + "F3", {"entities" : qUnion([Q0]), "depth" : 2 * mm, "offsetDistance" : 25.4 * mm});
        }
        {
            var Q0;
            Q0=qCreatedBy(makeId("Top.planeOp"),FACE);
            var sketch = newSketch(context, id + "F4", { "sketchPlane" : qUnion([Q0])});
            skLineSegment(sketch, "E41.bottom", {"start": v(28.58, 15.88) * mm, "end": v(-28.57, 15.88) * mm});
            skLineSegment(sketch, "E41.top", {"start": v(28.57, -15.88) * mm, "end": v(-28.58, -15.88) * mm});
            skLineSegment(sketch, "E41.left", {"start": v(28.58, 15.88) * mm, "end": v(28.57, -15.88) * mm});
            skLineSegment(sketch, "E41.right", {"start": v(-28.57, 15.88) * mm, "end": v(-28.58, -15.88) * mm});
            skPoint(sketch, "E41.middle", {"position": v(0, 0) * mm});
            skSolve(sketch);
        }
        {
            var Q0;
            Q0 = qSketchRegion(id + "F4", true);
            extrude(context, id + "F5", {"entities" : qUnion([Q0]), "depth" : .5 * mm, "offsetDistance" : 25.4 * mm});
        }
    });
